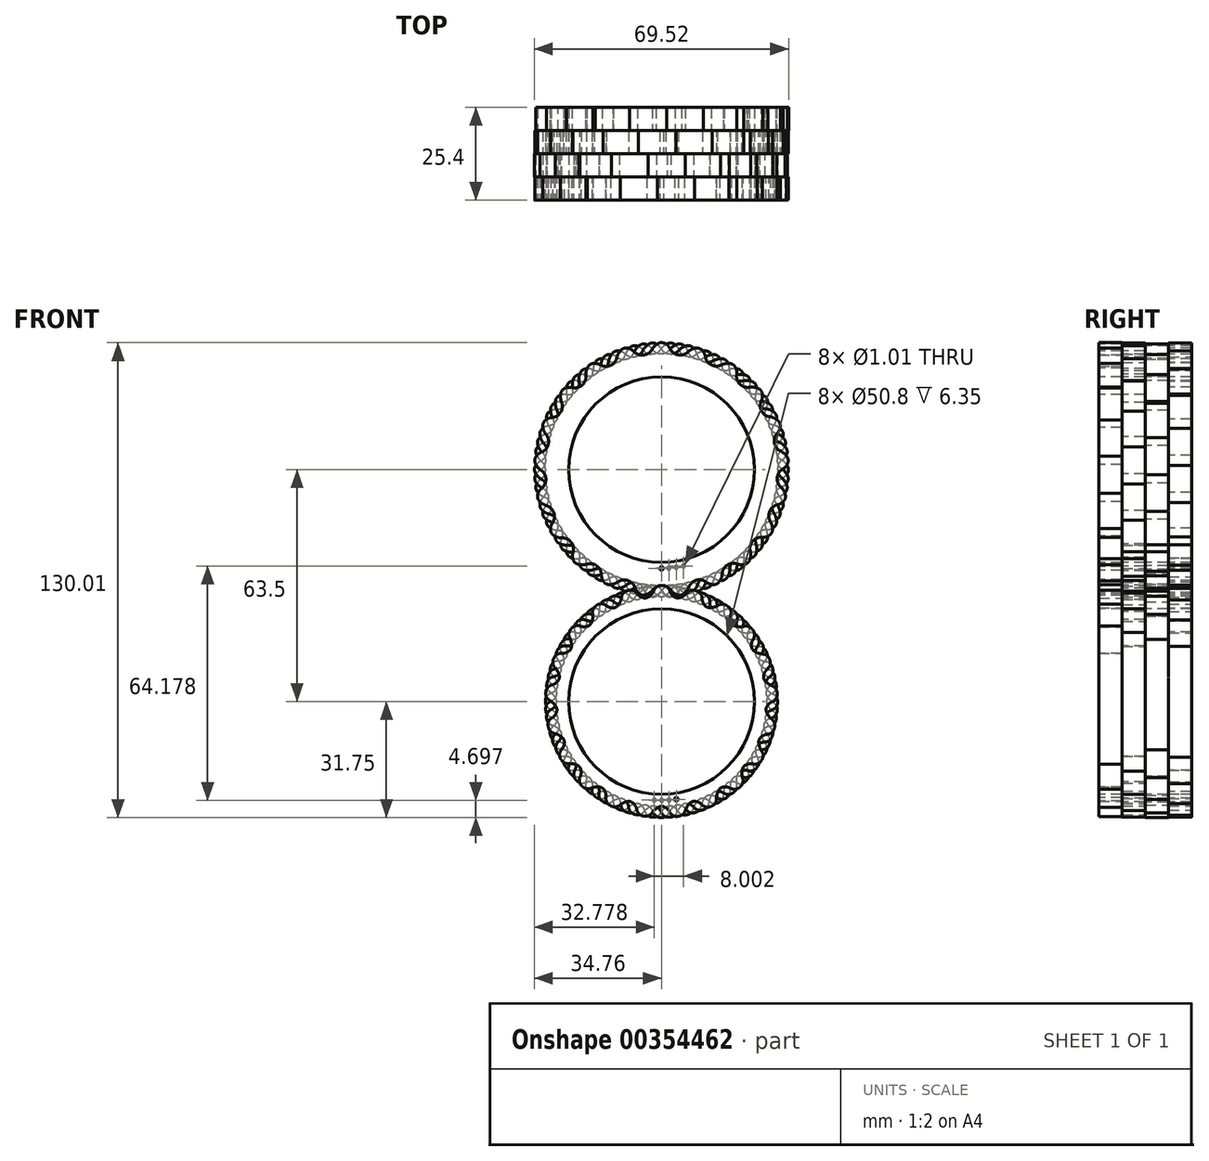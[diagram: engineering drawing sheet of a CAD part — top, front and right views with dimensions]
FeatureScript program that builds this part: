
annotation { "Feature Type Name" : "Feature", "Feature Type Description" : "" }
export const myFeature = defineFeature(function(context is Context, id is Id, definition is map)
    precondition{}
    {
        {
            var Q0;
            Q0=qCreatedBy(makeId("Front.planeOp"),FACE);
            var sketch = newSketch(context, id + "F0", { "sketchPlane" : qUnion([Q0])});
            skCircle(sketch, "E0", {"center": v(0, 0) * mm, "radius": 31.75 * mm});
            skCircle(sketch, "E1", {"center": v(0, 0) * mm, "radius": 25.4 * mm});
            skArc(sketch, "E2", {"start": v(0, 34.92) * mm, "mid": v(-2.02, 33.68) * mm, "end": v(-3.17, 31.6) * mm});
            skArc(sketch, "E3", {"start": v(0, 28.57) * mm, "mid": v(1.96, 29.69) * mm, "end": v(3.17, 31.6) * mm});
            skLineSegment(sketch, "E4", {"start": v(1.98, 33.73) * mm, "end": v(3.17, 31.6) * mm});
            skArc(sketch, "E5", {"start": v(-2.01, 29.74) * mm, "mid": v(-2.47, 30.74) * mm, "end": v(-3.17, 31.6) * mm});
            skArc(sketch, "E6", {"start": v(1.98, 33.73) * mm, "mid": v(1.06, 34.45) * mm, "end": v(0, 34.92) * mm});
            skArc(sketch, "E7", {"start": v(-2.01, 29.74) * mm, "mid": v(-1.08, 29.03) * mm, "end": v(0, 28.57) * mm});
            skArc(sketch, "E8.1.0", {"start": v(-10.3, 33.37) * mm, "mid": v(-11.86, 31.58) * mm, "end": v(-12.34, 29.25) * mm});
            skArc(sketch, "E8.1.1", {"start": v(-8.05, 32.8) * mm, "mid": v(-9.14, 33.23) * mm, "end": v(-10.3, 33.37) * mm});
            skLineSegment(sketch, "E8.1.2", {"start": v(-8.05, 32.8) * mm, "end": v(-6.28, 31.12) * mm});
            skArc(sketch, "E8.1.3", {"start": v(-8.42, 27.3) * mm, "mid": v(-6.88, 28.95) * mm, "end": v(-6.28, 31.12) * mm});
            skArc(sketch, "E8.1.4", {"start": v(-10.69, 27.82) * mm, "mid": v(-9.59, 27.42) * mm, "end": v(-8.42, 27.3) * mm});
            skArc(sketch, "E8.1.5", {"start": v(-10.69, 27.82) * mm, "mid": v(-11.42, 28.65) * mm, "end": v(-12.34, 29.25) * mm});
            skArc(sketch, "E8.2.0", {"start": v(-19.67, 28.86) * mm, "mid": v(-20.64, 26.68) * mm, "end": v(-20.42, 24.32) * mm});
            skArc(sketch, "E8.2.1", {"start": v(-17.37, 28.98) * mm, "mid": v(-18.53, 29.06) * mm, "end": v(-19.67, 28.86) * mm});
            skLineSegment(sketch, "E8.2.2", {"start": v(-17.37, 28.98) * mm, "end": v(-15.18, 27.89) * mm});
            skArc(sketch, "E8.2.3", {"start": v(-16.1, 23.6) * mm, "mid": v(-15.1, 25.63) * mm, "end": v(-15.18, 27.89) * mm});
            skArc(sketch, "E8.2.4", {"start": v(-18.41, 23.44) * mm, "mid": v(-17.24, 23.38) * mm, "end": v(-16.1, 23.6) * mm});
            skArc(sketch, "E8.2.5", {"start": v(-18.41, 23.44) * mm, "mid": v(-19.36, 24) * mm, "end": v(-20.42, 24.32) * mm});
            skArc(sketch, "E9.3.3.0", {"start": v(-27.3, 21.78) * mm, "mid": v(-27.6, 19.41) * mm, "end": v(-26.68, 17.22) * mm});
            skArc(sketch, "E9.4.3.0", {"start": v(-25.14, 22.57) * mm, "mid": v(-26.27, 22.31) * mm, "end": v(-27.3, 21.78) * mm});
            skLineSegment(sketch, "E9.8.3.0", {"start": v(-25.14, 22.57) * mm, "end": v(-22.72, 22.18) * mm});
            skArc(sketch, "E9.11.3.0", {"start": v(-22.34, 17.82) * mm, "mid": v(-21.99, 20.04) * mm, "end": v(-22.72, 22.18) * mm});
            skArc(sketch, "E9.15.3.0", {"start": v(-24.5, 16.97) * mm, "mid": v(-23.37, 17.26) * mm, "end": v(-22.34, 17.82) * mm});
            skArc(sketch, "E9.19.3.0", {"start": v(-24.5, 16.97) * mm, "mid": v(-25.57, 17.24) * mm, "end": v(-26.68, 17.22) * mm});
            skArc(sketch, "E9.3.4.0", {"start": v(-32.51, 12.76) * mm, "mid": v(-32.09, 10.42) * mm, "end": v(-30.57, 8.59) * mm});
            skArc(sketch, "E9.4.4.0", {"start": v(-30.67, 14.16) * mm, "mid": v(-31.68, 13.58) * mm, "end": v(-32.51, 12.76) * mm});
            skLineSegment(sketch, "E9.8.4.0", {"start": v(-30.67, 14.16) * mm, "end": v(-28.25, 14.5) * mm});
            skArc(sketch, "E9.11.4.0", {"start": v(-26.6, 10.44) * mm, "mid": v(-26.92, 12.67) * mm, "end": v(-28.25, 14.5) * mm});
            skArc(sketch, "E9.15.4.0", {"start": v(-28.42, 9) * mm, "mid": v(-27.42, 9.6) * mm, "end": v(-26.6, 10.44) * mm});
            skArc(sketch, "E9.19.4.0", {"start": v(-28.42, 9) * mm, "mid": v(-29.52, 8.93) * mm, "end": v(-30.57, 8.59) * mm});
            skArc(sketch, "E9.3.5.0", {"start": v(-34.83, 2.6) * mm, "mid": v(-33.73, 0.5) * mm, "end": v(-31.74, -0.8) * mm});
            skArc(sketch, "E9.4.5.0", {"start": v(-33.48, 4.5) * mm, "mid": v(-34.27, 3.63) * mm, "end": v(-34.83, 2.6) * mm});
            skLineSegment(sketch, "E9.8.5.0", {"start": v(-33.48, 4.5) * mm, "end": v(-31.27, 5.52) * mm});
            skArc(sketch, "E9.11.5.0", {"start": v(-28.5, 2.14) * mm, "mid": v(-29.46, 4.17) * mm, "end": v(-31.27, 5.52) * mm});
            skArc(sketch, "E9.15.5.0", {"start": v(-29.8, 0.22) * mm, "mid": v(-29.03, 1.1) * mm, "end": v(-28.5, 2.14) * mm});
            skArc(sketch, "E9.19.5.0", {"start": v(-29.8, 0.22) * mm, "mid": v(-30.84, -0.16) * mm, "end": v(-31.74, -0.8) * mm});
            skArc(sketch, "E9.3.6.0", {"start": v(-34.05, -7.77) * mm, "mid": v(-32.38, -9.47) * mm, "end": v(-30.1, -10.12) * mm});
            skArc(sketch, "E9.4.6.0", {"start": v(-33.32, -5.58) * mm, "mid": v(-33.82, -6.63) * mm, "end": v(-34.05, -7.77) * mm});
            skLineSegment(sketch, "E9.8.6.0", {"start": v(-33.32, -5.58) * mm, "end": v(-31.5, -3.94) * mm});
            skArc(sketch, "E9.11.6.0", {"start": v(-27.86, -6.36) * mm, "mid": v(-29.38, -4.7) * mm, "end": v(-31.5, -3.94) * mm});
            skArc(sketch, "E9.15.6.0", {"start": v(-28.55, -8.58) * mm, "mid": v(-28.06, -7.51) * mm, "end": v(-27.86, -6.36) * mm});
            skArc(sketch, "E9.19.6.0", {"start": v(-28.55, -8.58) * mm, "mid": v(-29.42, -9.25) * mm, "end": v(-30.1, -10.12) * mm});
            skArc(sketch, "E9.3.7.0", {"start": v(-30.25, -17.46) * mm, "mid": v(-28.15, -18.6) * mm, "end": v(-25.77, -18.54) * mm});
            skArc(sketch, "E9.4.7.0", {"start": v(-30.2, -15.15) * mm, "mid": v(-30.37, -16.3) * mm, "end": v(-30.25, -17.46) * mm});
            skLineSegment(sketch, "E9.8.7.0", {"start": v(-30.2, -15.15) * mm, "end": v(-28.94, -13.05) * mm});
            skArc(sketch, "E9.11.7.0", {"start": v(-24.75, -14.29) * mm, "mid": v(-26.7, -13.15) * mm, "end": v(-28.94, -13.05) * mm});
            skArc(sketch, "E9.15.7.0", {"start": v(-24.75, -16.61) * mm, "mid": v(-24.6, -15.45) * mm, "end": v(-24.75, -14.29) * mm});
            skArc(sketch, "E9.19.7.0", {"start": v(-24.75, -16.61) * mm, "mid": v(-25.39, -17.5) * mm, "end": v(-25.77, -18.54) * mm});
            skArc(sketch, "E9.3.8.0", {"start": v(-23.76, -25.6) * mm, "mid": v(-21.42, -26.06) * mm, "end": v(-19.16, -25.31) * mm});
            skArc(sketch, "E9.4.8.0", {"start": v(-24.39, -23.38) * mm, "mid": v(-24.21, -24.53) * mm, "end": v(-23.76, -25.6) * mm});
            skLineSegment(sketch, "E9.8.8.0", {"start": v(-24.39, -23.38) * mm, "end": v(-23.81, -21) * mm});
            skArc(sketch, "E9.11.8.0", {"start": v(-19.44, -20.95) * mm, "mid": v(-21.63, -20.43) * mm, "end": v(-23.81, -21) * mm});
            skArc(sketch, "E9.15.8.0", {"start": v(-18.75, -23.17) * mm, "mid": v(-18.95, -22.01) * mm, "end": v(-19.44, -20.95) * mm});
            skArc(sketch, "E9.19.8.0", {"start": v(-18.75, -23.17) * mm, "mid": v(-19.1, -24.21) * mm, "end": v(-19.16, -25.31) * mm});
            skArc(sketch, "E9.3.9.0", {"start": v(-15.15, -31.47) * mm, "mid": v(-12.79, -31.22) * mm, "end": v(-10.85, -29.84) * mm});
            skArc(sketch, "E9.4.9.0", {"start": v(-16.41, -29.53) * mm, "mid": v(-15.9, -30.58) * mm, "end": v(-15.15, -31.47) * mm});
            skLineSegment(sketch, "E9.8.9.0", {"start": v(-16.41, -29.53) * mm, "end": v(-16.56, -27.09) * mm});
            skArc(sketch, "E9.11.9.0", {"start": v(-12.4, -25.75) * mm, "mid": v(-14.65, -25.9) * mm, "end": v(-16.56, -27.09) * mm});
            skArc(sketch, "E9.15.9.0", {"start": v(-11.1, -27.67) * mm, "mid": v(-11.62, -26.62) * mm, "end": v(-12.4, -25.75) * mm});
            skArc(sketch, "E9.19.9.0", {"start": v(-11.1, -27.67) * mm, "mid": v(-11.11, -28.77) * mm, "end": v(-10.85, -29.84) * mm});
            skArc(sketch, "E9.3.10.0", {"start": v(-5.2, -34.53) * mm, "mid": v(-3.02, -33.6) * mm, "end": v(-1.57, -31.71) * mm});
            skArc(sketch, "E9.4.10.0", {"start": v(-6.98, -33.05) * mm, "mid": v(-6.19, -33.9) * mm, "end": v(-5.2, -34.53) * mm});
            skLineSegment(sketch, "E9.8.10.0", {"start": v(-6.98, -33.05) * mm, "end": v(-7.84, -30.77) * mm});
            skArc(sketch, "E9.11.10.0", {"start": v(-4.26, -28.26) * mm, "mid": v(-6.36, -29.07) * mm, "end": v(-7.84, -30.77) * mm});
            skArc(sketch, "E9.15.10.0", {"start": v(-2.44, -29.7) * mm, "mid": v(-3.26, -28.87) * mm, "end": v(-4.26, -28.26) * mm});
            skArc(sketch, "E9.19.10.0", {"start": v(-2.44, -29.7) * mm, "mid": v(-2.14, -30.77) * mm, "end": v(-1.57, -31.71) * mm});
            skArc(sketch, "E9.3.11.0", {"start": v(5.2, -34.53) * mm, "mid": v(7.02, -33) * mm, "end": v(7.84, -30.77) * mm});
            skArc(sketch, "E9.4.11.0", {"start": v(3.07, -33.64) * mm, "mid": v(4.08, -34.22) * mm, "end": v(5.2, -34.53) * mm});
            skLineSegment(sketch, "E9.8.11.0", {"start": v(3.07, -33.64) * mm, "end": v(1.57, -31.71) * mm});
            skArc(sketch, "E9.11.11.0", {"start": v(4.26, -28.26) * mm, "mid": v(2.49, -29.65) * mm, "end": v(1.57, -31.71) * mm});
            skArc(sketch, "E9.15.11.0", {"start": v(6.42, -29.1) * mm, "mid": v(5.4, -28.54) * mm, "end": v(4.26, -28.26) * mm});
            skArc(sketch, "E9.19.11.0", {"start": v(6.42, -29.1) * mm, "mid": v(7.02, -30.03) * mm, "end": v(7.84, -30.77) * mm});
            skArc(sketch, "E9.3.12.0", {"start": v(15.15, -31.47) * mm, "mid": v(16.43, -29.46) * mm, "end": v(16.56, -27.09) * mm});
            skArc(sketch, "E9.4.12.0", {"start": v(12.85, -31.24) * mm, "mid": v(13.99, -31.5) * mm, "end": v(15.15, -31.47) * mm});
            skLineSegment(sketch, "E9.8.12.0", {"start": v(12.85, -31.24) * mm, "end": v(10.85, -29.84) * mm});
            skArc(sketch, "E9.11.12.0", {"start": v(12.4, -25.75) * mm, "mid": v(11.12, -27.6) * mm, "end": v(10.85, -29.84) * mm});
            skArc(sketch, "E9.15.12.0", {"start": v(14.72, -25.92) * mm, "mid": v(13.57, -25.69) * mm, "end": v(12.4, -25.75) * mm});
            skArc(sketch, "E9.19.12.0", {"start": v(14.72, -25.92) * mm, "mid": v(15.56, -26.63) * mm, "end": v(16.56, -27.09) * mm});
            skArc(sketch, "E9.3.13.0", {"start": v(23.76, -25.6) * mm, "mid": v(24.39, -23.3) * mm, "end": v(23.81, -21) * mm});
            skArc(sketch, "E9.4.13.0", {"start": v(21.5, -26.07) * mm, "mid": v(22.65, -25.98) * mm, "end": v(23.76, -25.6) * mm});
            skLineSegment(sketch, "E9.8.13.0", {"start": v(21.5, -26.07) * mm, "end": v(19.16, -25.31) * mm});
            skArc(sketch, "E9.11.13.0", {"start": v(19.44, -20.95) * mm, "mid": v(18.76, -23.1) * mm, "end": v(19.16, -25.31) * mm});
            skArc(sketch, "E9.15.13.0", {"start": v(21.7, -20.43) * mm, "mid": v(20.54, -20.55) * mm, "end": v(19.44, -20.95) * mm});
            skArc(sketch, "E9.19.13.0", {"start": v(21.7, -20.43) * mm, "mid": v(22.72, -20.86) * mm, "end": v(23.81, -21) * mm});
            skArc(sketch, "E9.3.14.0", {"start": v(30.25, -17.46) * mm, "mid": v(30.18, -15.08) * mm, "end": v(28.94, -13.05) * mm});
            skArc(sketch, "E9.4.14.0", {"start": v(28.22, -18.57) * mm, "mid": v(29.3, -18.15) * mm, "end": v(30.25, -17.46) * mm});
            skLineSegment(sketch, "E9.8.14.0", {"start": v(28.22, -18.57) * mm, "end": v(25.77, -18.54) * mm});
            skArc(sketch, "E9.11.14.0", {"start": v(24.75, -14.29) * mm, "mid": v(24.73, -16.54) * mm, "end": v(25.77, -18.54) * mm});
            skArc(sketch, "E9.15.14.0", {"start": v(26.76, -13.13) * mm, "mid": v(25.68, -13.58) * mm, "end": v(24.75, -14.29) * mm});
            skArc(sketch, "E9.19.14.0", {"start": v(26.76, -13.13) * mm, "mid": v(27.86, -13.23) * mm, "end": v(28.94, -13.05) * mm});
            skArc(sketch, "E9.3.15.0", {"start": v(34.05, -7.77) * mm, "mid": v(33.28, -5.52) * mm, "end": v(31.5, -3.94) * mm});
            skArc(sketch, "E9.4.15.0", {"start": v(32.44, -9.43) * mm, "mid": v(33.35, -8.7) * mm, "end": v(34.05, -7.77) * mm});
            skLineSegment(sketch, "E9.8.15.0", {"start": v(32.44, -9.43) * mm, "end": v(30.1, -10.12) * mm});
            skArc(sketch, "E9.11.15.0", {"start": v(27.86, -6.36) * mm, "mid": v(28.5, -8.52) * mm, "end": v(30.1, -10.12) * mm});
            skArc(sketch, "E9.15.15.0", {"start": v(29.44, -4.66) * mm, "mid": v(28.54, -5.4) * mm, "end": v(27.86, -6.36) * mm});
            skArc(sketch, "E9.19.15.0", {"start": v(29.44, -4.66) * mm, "mid": v(30.52, -4.43) * mm, "end": v(31.5, -3.94) * mm});
            skArc(sketch, "E9.3.16.0", {"start": v(34.83, 2.6) * mm, "mid": v(33.43, 4.54) * mm, "end": v(31.27, 5.52) * mm});
            skArc(sketch, "E9.4.16.0", {"start": v(33.78, 0.55) * mm, "mid": v(34.43, 1.51) * mm, "end": v(34.83, 2.6) * mm});
            skLineSegment(sketch, "E9.8.16.0", {"start": v(33.78, 0.55) * mm, "end": v(31.74, -0.8) * mm});
            skArc(sketch, "E9.11.16.0", {"start": v(28.5, 2.14) * mm, "mid": v(29.75, 0.26) * mm, "end": v(31.74, -0.8) * mm});
            skArc(sketch, "E9.15.16.0", {"start": v(29.5, 4.23) * mm, "mid": v(28.87, 3.25) * mm, "end": v(28.5, 2.14) * mm});
            skArc(sketch, "E9.19.16.0", {"start": v(29.5, 4.23) * mm, "mid": v(30.47, 4.76) * mm, "end": v(31.27, 5.52) * mm});
            skArc(sketch, "E9.3.17.0", {"start": v(32.51, 12.76) * mm, "mid": v(30.6, 14.19) * mm, "end": v(28.25, 14.5) * mm});
            skArc(sketch, "E9.4.17.0", {"start": v(32.12, 10.48) * mm, "mid": v(32.46, 11.6) * mm, "end": v(32.51, 12.76) * mm});
            skLineSegment(sketch, "E9.8.17.0", {"start": v(32.12, 10.48) * mm, "end": v(30.57, 8.59) * mm});
            skArc(sketch, "E9.11.17.0", {"start": v(26.6, 10.44) * mm, "mid": v(28.35, 9.02) * mm, "end": v(30.57, 8.59) * mm});
            skArc(sketch, "E9.15.17.0", {"start": v(26.95, 12.74) * mm, "mid": v(26.63, 11.61) * mm, "end": v(26.6, 10.44) * mm});
            skArc(sketch, "E9.19.17.0", {"start": v(26.95, 12.74) * mm, "mid": v(27.72, 13.53) * mm, "end": v(28.25, 14.5) * mm});
            skArc(sketch, "E9.3.18.0", {"start": v(27.3, 21.78) * mm, "mid": v(25.07, 22.58) * mm, "end": v(22.72, 22.18) * mm});
            skArc(sketch, "E9.4.18.0", {"start": v(27.6, 19.48) * mm, "mid": v(27.6, 20.65) * mm, "end": v(27.3, 21.78) * mm});
            skLineSegment(sketch, "E9.8.18.0", {"start": v(27.6, 19.48) * mm, "end": v(26.68, 17.22) * mm});
            skArc(sketch, "E9.11.18.0", {"start": v(22.34, 17.82) * mm, "mid": v(24.43, 16.98) * mm, "end": v(26.68, 17.22) * mm});
            skArc(sketch, "E9.15.18.0", {"start": v(22, 20.11) * mm, "mid": v(22.02, 18.94) * mm, "end": v(22.34, 17.82) * mm});
            skArc(sketch, "E9.19.18.0", {"start": v(22, 20.11) * mm, "mid": v(22.5, 21.1) * mm, "end": v(22.72, 22.18) * mm});
            skArc(sketch, "E9.3.19.0", {"start": v(19.67, 28.86) * mm, "mid": v(17.3, 28.96) * mm, "end": v(15.18, 27.89) * mm});
            skArc(sketch, "E9.4.19.0", {"start": v(20.63, 26.75) * mm, "mid": v(20.28, 27.86) * mm, "end": v(19.67, 28.86) * mm});
            skLineSegment(sketch, "E9.8.19.0", {"start": v(20.63, 26.75) * mm, "end": v(20.42, 24.32) * mm});
            skArc(sketch, "E9.11.19.0", {"start": v(16.1, 23.6) * mm, "mid": v(18.34, 23.43) * mm, "end": v(20.42, 24.32) * mm});
            skArc(sketch, "E9.15.19.0", {"start": v(15.1, 25.7) * mm, "mid": v(15.46, 24.6) * mm, "end": v(16.1, 23.6) * mm});
            skArc(sketch, "E9.19.19.0", {"start": v(15.1, 25.7) * mm, "mid": v(15.28, 26.8) * mm, "end": v(15.18, 27.89) * mm});
            skArc(sketch, "E9.3.20.0", {"start": v(10.3, 33.37) * mm, "mid": v(8, 32.78) * mm, "end": v(6.28, 31.12) * mm});
            skArc(sketch, "E9.4.20.0", {"start": v(11.83, 31.64) * mm, "mid": v(11.17, 32.6) * mm, "end": v(10.3, 33.37) * mm});
            skLineSegment(sketch, "E9.8.20.0", {"start": v(11.83, 31.64) * mm, "end": v(12.34, 29.25) * mm});
            skArc(sketch, "E9.11.20.0", {"start": v(8.42, 27.3) * mm, "mid": v(10.62, 27.8) * mm, "end": v(12.34, 29.25) * mm});
            skArc(sketch, "E9.15.20.0", {"start": v(6.84, 29.01) * mm, "mid": v(7.53, 28.06) * mm, "end": v(8.42, 27.3) * mm});
            skArc(sketch, "E9.19.20.0", {"start": v(6.84, 29.01) * mm, "mid": v(6.7, 30.1) * mm, "end": v(6.28, 31.12) * mm});
            skArc(sketch, "E10", {"start": v(0.11, 34.89) * mm, "mid": v(-0.54, 34.69) * mm, "end": v(-1.15, 34.4) * mm});
            skArc(sketch, "E11.1.0", {"start": v(-10.18, 33.37) * mm, "mid": v(-10.74, 32.99) * mm, "end": v(-11.24, 32.53) * mm});
            skArc(sketch, "E11.2.0", {"start": v(-19.56, 28.89) * mm, "mid": v(-19.99, 28.36) * mm, "end": v(-20.33, 27.77) * mm});
            skArc(sketch, "E11.3.0", {"start": v(-27.2, 21.84) * mm, "mid": v(-27.46, 21.2) * mm, "end": v(-27.6, 20.54) * mm});
            skArc(sketch, "E11.4.0", {"start": v(-32.44, 12.85) * mm, "mid": v(-32.49, 12.17) * mm, "end": v(-32.44, 11.5) * mm});
            skArc(sketch, "E11.5.0", {"start": v(-34.78, 2.72) * mm, "mid": v(-34.63, 2.05) * mm, "end": v(-34.38, 1.42) * mm});
            skArc(sketch, "E11.6.0", {"start": v(-34.04, -7.66) * mm, "mid": v(-33.7, -8.24) * mm, "end": v(-33.28, -8.78) * mm});
            skArc(sketch, "E11.7.0", {"start": v(-30.27, -17.35) * mm, "mid": v(-29.77, -17.81) * mm, "end": v(-29.21, -18.2) * mm});
            skArc(sketch, "E11.8.0", {"start": v(-23.81, -25.5) * mm, "mid": v(-23.2, -25.8) * mm, "end": v(-22.55, -26) * mm});
            skArc(sketch, "E11.9.0", {"start": v(-15.24, -31.39) * mm, "mid": v(-14.56, -31.49) * mm, "end": v(-13.89, -31.49) * mm});
            skArc(sketch, "E11.10.0", {"start": v(-5.3, -34.48) * mm, "mid": v(-4.64, -34.38) * mm, "end": v(-3.99, -34.18) * mm});
            skArc(sketch, "E11.11.0", {"start": v(5.1, -34.52) * mm, "mid": v(5.7, -34.22) * mm, "end": v(6.27, -33.84) * mm});
            skArc(sketch, "E11.12.0", {"start": v(15.04, -31.48) * mm, "mid": v(15.54, -31.02) * mm, "end": v(15.96, -30.49) * mm});
            skArc(sketch, "E11.13.0", {"start": v(23.65, -25.65) * mm, "mid": v(23.99, -25.06) * mm, "end": v(24.24, -24.43) * mm});
            skArc(sketch, "E11.14.0", {"start": v(30.16, -17.54) * mm, "mid": v(30.31, -16.88) * mm, "end": v(30.36, -16.2) * mm});
            skArc(sketch, "E11.15.0", {"start": v(34, -7.87) * mm, "mid": v(33.94, -7.2) * mm, "end": v(33.79, -6.53) * mm});
            skArc(sketch, "E11.16.0", {"start": v(34.8, 2.5) * mm, "mid": v(34.55, 3.13) * mm, "end": v(34.21, 3.72) * mm});
            skArc(sketch, "E11.17.0", {"start": v(32.52, 12.64) * mm, "mid": v(32.1, 13.17) * mm, "end": v(31.6, 13.64) * mm});
            skArc(sketch, "E11.18.0", {"start": v(27.35, 21.67) * mm, "mid": v(26.78, 22.05) * mm, "end": v(26.17, 22.34) * mm});
            skArc(sketch, "E11.19.0", {"start": v(19.75, 28.77) * mm, "mid": v(19.1, 28.96) * mm, "end": v(18.42, 29.07) * mm});
            skArc(sketch, "E11.20.0", {"start": v(10.39, 33.3) * mm, "mid": v(9.7, 33.3) * mm, "end": v(9.04, 33.2) * mm});
            skCircle(sketch, "E12", {"center": v(0, -27.05) * mm, "radius": 0.5 * mm});
            skSolve(sketch);
        }
        {
            var Q0;
            Q0=makeQuery(id+"F0.imprint","IMPRINT",FACE,{"disambiguationData":[TD([[makeQuery(id+"F0.imprint","IMPRINT",EDGE,{"derivedFrom":sQuery(id+"F0.wireOp",EDGE,"E1")}),-1.0]])]});
            var Q1;
            Q1=makeQuery(id+"F0.imprint","IMPRINT",FACE,{"disambiguationData":[TD([[makeQuery(id+"F0.imprint","IMPRINT",EDGE,{"derivedFrom":sQuery(id+"F0.wireOp",EDGE,"Dn7gvafj-PEvj-KMcr-wK7N-n03crIEQc72X")}),1.0]])]});
            extrude(context, id + "F1", {"entities" : qUnion([Q0, Q1]), "oppositeDirection" : true, "depth" : 6.35 * mm});
        }
        {
            var Q0;
            {var subQ2=sQuery(id+"F0.wireOp",EDGE,"E3");Q0=makeQuery(id+"F0.imprint","IMPRINT",FACE,{"disambiguationData":[TD([[makeQuery(id+"F0.imprint","IMPRINT",EDGE,{"derivedFrom":subQ2}),1.0]])]});}
            var Q1;
            {var subQ2=sQuery(id+"F0.wireOp",EDGE,"E9.11.20.0");Q1=makeQuery(id+"F0.imprint","IMPRINT",FACE,{"disambiguationData":[TD([[makeQuery(id+"F0.imprint","IMPRINT",EDGE,{"derivedFrom":subQ2}),1.0]])]});}
            var Q2;
            {var subQ2=sQuery(id+"F0.wireOp",EDGE,"E9.11.19.0");Q2=makeQuery(id+"F0.imprint","IMPRINT",FACE,{"disambiguationData":[TD([[makeQuery(id+"F0.imprint","IMPRINT",EDGE,{"derivedFrom":subQ2}),1.0]])]});}
            var Q3;
            {var subQ2=sQuery(id+"F0.wireOp",EDGE,"E9.11.18.0");Q3=makeQuery(id+"F0.imprint","IMPRINT",FACE,{"disambiguationData":[TD([[makeQuery(id+"F0.imprint","IMPRINT",EDGE,{"derivedFrom":subQ2}),1.0]])]});}
            var Q4;
            {var subQ2=sQuery(id+"F0.wireOp",EDGE,"E8.1.3");Q4=makeQuery(id+"F0.imprint","IMPRINT",FACE,{"disambiguationData":[TD([[makeQuery(id+"F0.imprint","IMPRINT",EDGE,{"derivedFrom":subQ2}),1.0]])]});}
            var Q5;
            {var subQ2=sQuery(id+"F0.wireOp",EDGE,"E8.2.3");Q5=makeQuery(id+"F0.imprint","IMPRINT",FACE,{"disambiguationData":[TD([[makeQuery(id+"F0.imprint","IMPRINT",EDGE,{"derivedFrom":subQ2}),1.0]])]});}
            var Q6;
            {var subQ2=sQuery(id+"F0.wireOp",EDGE,"E9.11.3.0");Q6=makeQuery(id+"F0.imprint","IMPRINT",FACE,{"disambiguationData":[TD([[makeQuery(id+"F0.imprint","IMPRINT",EDGE,{"derivedFrom":subQ2}),1.0]])]});}
            var Q7;
            {var subQ2=sQuery(id+"F0.wireOp",EDGE,"E9.11.4.0");Q7=makeQuery(id+"F0.imprint","IMPRINT",FACE,{"disambiguationData":[TD([[makeQuery(id+"F0.imprint","IMPRINT",EDGE,{"derivedFrom":subQ2}),1.0]])]});}
            var Q8;
            {var subQ2=sQuery(id+"F0.wireOp",EDGE,"E9.11.5.0");Q8=makeQuery(id+"F0.imprint","IMPRINT",FACE,{"disambiguationData":[TD([[makeQuery(id+"F0.imprint","IMPRINT",EDGE,{"derivedFrom":subQ2}),1.0]])]});}
            var Q9;
            {var subQ2=sQuery(id+"F0.wireOp",EDGE,"E9.11.6.0");Q9=makeQuery(id+"F0.imprint","IMPRINT",FACE,{"disambiguationData":[TD([[makeQuery(id+"F0.imprint","IMPRINT",EDGE,{"derivedFrom":subQ2}),1.0]])]});}
            var Q10;
            {var subQ2=sQuery(id+"F0.wireOp",EDGE,"E9.11.17.0");Q10=makeQuery(id+"F0.imprint","IMPRINT",FACE,{"disambiguationData":[TD([[makeQuery(id+"F0.imprint","IMPRINT",EDGE,{"derivedFrom":subQ2}),1.0]])]});}
            var Q11;
            {var subQ2=sQuery(id+"F0.wireOp",EDGE,"E9.11.16.0");Q11=makeQuery(id+"F0.imprint","IMPRINT",FACE,{"disambiguationData":[TD([[makeQuery(id+"F0.imprint","IMPRINT",EDGE,{"derivedFrom":subQ2}),1.0]])]});}
            var Q12;
            {var subQ2=sQuery(id+"F0.wireOp",EDGE,"E9.11.15.0");Q12=makeQuery(id+"F0.imprint","IMPRINT",FACE,{"disambiguationData":[TD([[makeQuery(id+"F0.imprint","IMPRINT",EDGE,{"derivedFrom":subQ2}),1.0]])]});}
            var Q13;
            {var subQ2=sQuery(id+"F0.wireOp",EDGE,"E9.11.7.0");Q13=makeQuery(id+"F0.imprint","IMPRINT",FACE,{"disambiguationData":[TD([[makeQuery(id+"F0.imprint","IMPRINT",EDGE,{"derivedFrom":subQ2}),1.0]])]});}
            var Q14;
            {var subQ2=sQuery(id+"F0.wireOp",EDGE,"E9.11.8.0");Q14=makeQuery(id+"F0.imprint","IMPRINT",FACE,{"disambiguationData":[TD([[makeQuery(id+"F0.imprint","IMPRINT",EDGE,{"derivedFrom":subQ2}),1.0]])]});}
            var Q15;
            {var subQ2=sQuery(id+"F0.wireOp",EDGE,"E9.11.9.0");Q15=makeQuery(id+"F0.imprint","IMPRINT",FACE,{"disambiguationData":[TD([[makeQuery(id+"F0.imprint","IMPRINT",EDGE,{"derivedFrom":subQ2}),1.0]])]});}
            var Q16;
            {var subQ2=sQuery(id+"F0.wireOp",EDGE,"E9.11.10.0");Q16=makeQuery(id+"F0.imprint","IMPRINT",FACE,{"disambiguationData":[TD([[makeQuery(id+"F0.imprint","IMPRINT",EDGE,{"derivedFrom":subQ2}),1.0]])]});}
            var Q17;
            {var subQ2=sQuery(id+"F0.wireOp",EDGE,"E9.11.11.0");Q17=makeQuery(id+"F0.imprint","IMPRINT",FACE,{"disambiguationData":[TD([[makeQuery(id+"F0.imprint","IMPRINT",EDGE,{"derivedFrom":subQ2}),1.0]])]});}
            var Q18;
            {var subQ2=sQuery(id+"F0.wireOp",EDGE,"E9.11.12.0");Q18=makeQuery(id+"F0.imprint","IMPRINT",FACE,{"disambiguationData":[TD([[makeQuery(id+"F0.imprint","IMPRINT",EDGE,{"derivedFrom":subQ2}),1.0]])]});}
            var Q19;
            {var subQ2=sQuery(id+"F0.wireOp",EDGE,"E9.11.13.0");Q19=makeQuery(id+"F0.imprint","IMPRINT",FACE,{"disambiguationData":[TD([[makeQuery(id+"F0.imprint","IMPRINT",EDGE,{"derivedFrom":subQ2}),1.0]])]});}
            var Q20;
            {var subQ2=sQuery(id+"F0.wireOp",EDGE,"E9.11.14.0");Q20=makeQuery(id+"F0.imprint","IMPRINT",FACE,{"disambiguationData":[TD([[makeQuery(id+"F0.imprint","IMPRINT",EDGE,{"derivedFrom":subQ2}),1.0]])]});}
            var Q21;
            Q21=makeQuery(id+"F0.imprint","IMPRINT",FACE,{"disambiguationData":[TD([[makeQuery(id+"F0.imprint","IMPRINT",EDGE,{"derivedFrom":sQuery(id+"F0.wireOp",EDGE,"E1")}),-1.0]])]});
            var Q22;
            {var subQ1=sQuery(id+"F0.wireOp",EDGE,"E4");Q22=makeQuery(id+"F0.imprint","IMPRINT",FACE,{"disambiguationData":[TD([[makeQuery(id+"F0.imprint","IMPRINT",EDGE,{"derivedFrom":subQ1}),-1.0]])]});}
            var Q23;
            {var subQ0=sQuery(id+"F0.wireOp",EDGE,"E9.8.20.0");Q23=makeQuery(id+"F0.imprint","IMPRINT",FACE,{"disambiguationData":[TD([[makeQuery(id+"F0.imprint","IMPRINT",EDGE,{"derivedFrom":subQ0}),-1.0]])]});}
            var Q24;
            {var subQ0=sQuery(id+"F0.wireOp",EDGE,"E9.8.19.0");Q24=makeQuery(id+"F0.imprint","IMPRINT",FACE,{"disambiguationData":[TD([[makeQuery(id+"F0.imprint","IMPRINT",EDGE,{"derivedFrom":subQ0}),-1.0]])]});}
            var Q25;
            {var subQ0=sQuery(id+"F0.wireOp",EDGE,"E9.8.18.0");Q25=makeQuery(id+"F0.imprint","IMPRINT",FACE,{"disambiguationData":[TD([[makeQuery(id+"F0.imprint","IMPRINT",EDGE,{"derivedFrom":subQ0}),-1.0]])]});}
            var Q26;
            {var subQ0=sQuery(id+"F0.wireOp",EDGE,"E9.8.17.0");Q26=makeQuery(id+"F0.imprint","IMPRINT",FACE,{"disambiguationData":[TD([[makeQuery(id+"F0.imprint","IMPRINT",EDGE,{"derivedFrom":subQ0}),-1.0]])]});}
            var Q27;
            {var subQ0=sQuery(id+"F0.wireOp",EDGE,"E9.8.16.0");Q27=makeQuery(id+"F0.imprint","IMPRINT",FACE,{"disambiguationData":[TD([[makeQuery(id+"F0.imprint","IMPRINT",EDGE,{"derivedFrom":subQ0}),-1.0]])]});}
            var Q28;
            {var subQ0=sQuery(id+"F0.wireOp",EDGE,"E9.8.15.0");Q28=makeQuery(id+"F0.imprint","IMPRINT",FACE,{"disambiguationData":[TD([[makeQuery(id+"F0.imprint","IMPRINT",EDGE,{"derivedFrom":subQ0}),-1.0]])]});}
            var Q29;
            {var subQ0=sQuery(id+"F0.wireOp",EDGE,"E9.8.14.0");Q29=makeQuery(id+"F0.imprint","IMPRINT",FACE,{"disambiguationData":[TD([[makeQuery(id+"F0.imprint","IMPRINT",EDGE,{"derivedFrom":subQ0}),-1.0]])]});}
            var Q30;
            {var subQ0=sQuery(id+"F0.wireOp",EDGE,"E9.8.13.0");Q30=makeQuery(id+"F0.imprint","IMPRINT",FACE,{"disambiguationData":[TD([[makeQuery(id+"F0.imprint","IMPRINT",EDGE,{"derivedFrom":subQ0}),-1.0]])]});}
            var Q31;
            {var subQ0=sQuery(id+"F0.wireOp",EDGE,"E9.8.12.0");Q31=makeQuery(id+"F0.imprint","IMPRINT",FACE,{"disambiguationData":[TD([[makeQuery(id+"F0.imprint","IMPRINT",EDGE,{"derivedFrom":subQ0}),-1.0]])]});}
            var Q32;
            {var subQ0=sQuery(id+"F0.wireOp",EDGE,"E9.8.11.0");Q32=makeQuery(id+"F0.imprint","IMPRINT",FACE,{"disambiguationData":[TD([[makeQuery(id+"F0.imprint","IMPRINT",EDGE,{"derivedFrom":subQ0}),-1.0]])]});}
            var Q33;
            {var subQ0=sQuery(id+"F0.wireOp",EDGE,"E9.8.10.0");Q33=makeQuery(id+"F0.imprint","IMPRINT",FACE,{"disambiguationData":[TD([[makeQuery(id+"F0.imprint","IMPRINT",EDGE,{"derivedFrom":subQ0}),-1.0]])]});}
            var Q34;
            {var subQ0=sQuery(id+"F0.wireOp",EDGE,"E9.8.9.0");Q34=makeQuery(id+"F0.imprint","IMPRINT",FACE,{"disambiguationData":[TD([[makeQuery(id+"F0.imprint","IMPRINT",EDGE,{"derivedFrom":subQ0}),-1.0]])]});}
            var Q35;
            {var subQ0=sQuery(id+"F0.wireOp",EDGE,"E9.8.8.0");Q35=makeQuery(id+"F0.imprint","IMPRINT",FACE,{"disambiguationData":[TD([[makeQuery(id+"F0.imprint","IMPRINT",EDGE,{"derivedFrom":subQ0}),-1.0]])]});}
            var Q36;
            {var subQ0=sQuery(id+"F0.wireOp",EDGE,"E9.8.7.0");Q36=makeQuery(id+"F0.imprint","IMPRINT",FACE,{"disambiguationData":[TD([[makeQuery(id+"F0.imprint","IMPRINT",EDGE,{"derivedFrom":subQ0}),-1.0]])]});}
            var Q37;
            {var subQ0=sQuery(id+"F0.wireOp",EDGE,"E9.8.6.0");Q37=makeQuery(id+"F0.imprint","IMPRINT",FACE,{"disambiguationData":[TD([[makeQuery(id+"F0.imprint","IMPRINT",EDGE,{"derivedFrom":subQ0}),-1.0]])]});}
            var Q38;
            {var subQ0=sQuery(id+"F0.wireOp",EDGE,"E9.8.5.0");Q38=makeQuery(id+"F0.imprint","IMPRINT",FACE,{"disambiguationData":[TD([[makeQuery(id+"F0.imprint","IMPRINT",EDGE,{"derivedFrom":subQ0}),-1.0]])]});}
            var Q39;
            {var subQ0=sQuery(id+"F0.wireOp",EDGE,"E9.8.4.0");Q39=makeQuery(id+"F0.imprint","IMPRINT",FACE,{"disambiguationData":[TD([[makeQuery(id+"F0.imprint","IMPRINT",EDGE,{"derivedFrom":subQ0}),-1.0]])]});}
            var Q40;
            {var subQ0=sQuery(id+"F0.wireOp",EDGE,"E9.8.3.0");Q40=makeQuery(id+"F0.imprint","IMPRINT",FACE,{"disambiguationData":[TD([[makeQuery(id+"F0.imprint","IMPRINT",EDGE,{"derivedFrom":subQ0}),-1.0]])]});}
            var Q41;
            {var subQ0=sQuery(id+"F0.wireOp",EDGE,"E8.2.2");Q41=makeQuery(id+"F0.imprint","IMPRINT",FACE,{"disambiguationData":[TD([[makeQuery(id+"F0.imprint","IMPRINT",EDGE,{"derivedFrom":subQ0}),-1.0]])]});}
            var Q42;
            {var subQ0=sQuery(id+"F0.wireOp",EDGE,"E8.1.2");Q42=makeQuery(id+"F0.imprint","IMPRINT",FACE,{"disambiguationData":[TD([[makeQuery(id+"F0.imprint","IMPRINT",EDGE,{"derivedFrom":subQ0}),-1.0]])]});}
            extrude(context, id + "F2", {"entities" : qUnion([Q0, Q1, Q2, Q3, Q4, Q5, Q6, Q7, Q8, Q9, Q10, Q11, Q12, Q13, Q14, Q15, Q16, Q17, Q18, Q19, Q20, Q21, Q22, Q23, Q24, Q25, Q26, Q27, Q28, Q29, Q30, Q31, Q32, Q33, Q34, Q35, Q36, Q37, Q38, Q39, Q40, Q41, Q42]), "oppositeDirection" : true, "depth" : 6.35 * mm});
        }
        {
            var Q0;
            Q0=makeQuery(id+"F2.opExtrude","SWEPT_EDGE",EDGE,{"disambiguationData":[OSD([sQuery(id+"F0.wireOp",EDGE,"E6"),sQuery(id+"F0.wireOp",EDGE,"E10")])]});
            var Q1;
            Q1=makeQuery(id+"F2.opExtrude","SWEPT_EDGE",EDGE,{"disambiguationData":[OSD([sQuery(id+"F0.wireOp",EDGE,"E8.1.1"),sQuery(id+"F0.wireOp",EDGE,"E11.1.0")])]});
            var Q2;
            Q2=makeQuery(id+"F2.opExtrude","SWEPT_EDGE",EDGE,{"disambiguationData":[OSD([sQuery(id+"F0.wireOp",EDGE,"E8.2.1"),sQuery(id+"F0.wireOp",EDGE,"E11.2.0")])]});
            var Q3;
            Q3=makeQuery(id+"F2.opExtrude","SWEPT_EDGE",EDGE,{"disambiguationData":[OSD([sQuery(id+"F0.wireOp",EDGE,"E9.4.3.0"),sQuery(id+"F0.wireOp",EDGE,"E11.3.0")])]});
            var Q4;
            Q4=makeQuery(id+"F2.opExtrude","SWEPT_EDGE",EDGE,{"disambiguationData":[OSD([sQuery(id+"F0.wireOp",EDGE,"E9.4.20.0"),sQuery(id+"F0.wireOp",EDGE,"E11.20.0")])]});
            var Q5;
            Q5=makeQuery(id+"F2.opExtrude","SWEPT_EDGE",EDGE,{"disambiguationData":[OSD([sQuery(id+"F0.wireOp",EDGE,"E9.4.19.0"),sQuery(id+"F0.wireOp",EDGE,"E11.19.0")])]});
            var Q6;
            Q6=makeQuery(id+"F2.opExtrude","SWEPT_EDGE",EDGE,{"disambiguationData":[OSD([sQuery(id+"F0.wireOp",EDGE,"E9.4.18.0"),sQuery(id+"F0.wireOp",EDGE,"E11.18.0")])]});
            var Q7;
            Q7=makeQuery(id+"F2.opExtrude","SWEPT_EDGE",EDGE,{"disambiguationData":[OSD([sQuery(id+"F0.wireOp",EDGE,"E9.4.17.0"),sQuery(id+"F0.wireOp",EDGE,"E11.17.0")])]});
            var Q8;
            Q8=makeQuery(id+"F2.opExtrude","SWEPT_EDGE",EDGE,{"disambiguationData":[OSD([sQuery(id+"F0.wireOp",EDGE,"E9.4.16.0"),sQuery(id+"F0.wireOp",EDGE,"E11.16.0")])]});
            var Q9;
            Q9=makeQuery(id+"F2.opExtrude","SWEPT_EDGE",EDGE,{"disambiguationData":[OSD([sQuery(id+"F0.wireOp",EDGE,"E9.4.15.0"),sQuery(id+"F0.wireOp",EDGE,"E11.15.0")])]});
            var Q10;
            Q10=makeQuery(id+"F2.opExtrude","SWEPT_EDGE",EDGE,{"disambiguationData":[OSD([sQuery(id+"F0.wireOp",EDGE,"E9.4.4.0"),sQuery(id+"F0.wireOp",EDGE,"E11.4.0")])]});
            var Q11;
            Q11=makeQuery(id+"F2.opExtrude","SWEPT_EDGE",EDGE,{"disambiguationData":[OSD([sQuery(id+"F0.wireOp",EDGE,"E9.4.5.0"),sQuery(id+"F0.wireOp",EDGE,"E11.5.0")])]});
            var Q12;
            Q12=makeQuery(id+"F2.opExtrude","SWEPT_EDGE",EDGE,{"disambiguationData":[OSD([sQuery(id+"F0.wireOp",EDGE,"E9.4.6.0"),sQuery(id+"F0.wireOp",EDGE,"E11.6.0")])]});
            var Q13;
            Q13=makeQuery(id+"F2.opExtrude","SWEPT_EDGE",EDGE,{"disambiguationData":[OSD([sQuery(id+"F0.wireOp",EDGE,"E9.4.7.0"),sQuery(id+"F0.wireOp",EDGE,"E11.7.0")])]});
            var Q14;
            Q14=makeQuery(id+"F2.opExtrude","SWEPT_EDGE",EDGE,{"disambiguationData":[OSD([sQuery(id+"F0.wireOp",EDGE,"E9.4.14.0"),sQuery(id+"F0.wireOp",EDGE,"E11.14.0")])]});
            var Q15;
            Q15=makeQuery(id+"F2.opExtrude","SWEPT_EDGE",EDGE,{"disambiguationData":[OSD([sQuery(id+"F0.wireOp",EDGE,"E9.4.13.0"),sQuery(id+"F0.wireOp",EDGE,"E11.13.0")])]});
            var Q16;
            Q16=makeQuery(id+"F2.opExtrude","SWEPT_EDGE",EDGE,{"disambiguationData":[OSD([sQuery(id+"F0.wireOp",EDGE,"E9.4.12.0"),sQuery(id+"F0.wireOp",EDGE,"E11.12.0")])]});
            var Q17;
            Q17=makeQuery(id+"F2.opExtrude","SWEPT_EDGE",EDGE,{"disambiguationData":[OSD([sQuery(id+"F0.wireOp",EDGE,"E9.4.11.0"),sQuery(id+"F0.wireOp",EDGE,"E11.11.0")])]});
            var Q18;
            Q18=makeQuery(id+"F2.opExtrude","SWEPT_EDGE",EDGE,{"disambiguationData":[OSD([sQuery(id+"F0.wireOp",EDGE,"E9.4.10.0"),sQuery(id+"F0.wireOp",EDGE,"E11.10.0")])]});
            var Q19;
            Q19=makeQuery(id+"F2.opExtrude","SWEPT_EDGE",EDGE,{"disambiguationData":[OSD([sQuery(id+"F0.wireOp",EDGE,"E9.4.9.0"),sQuery(id+"F0.wireOp",EDGE,"E11.9.0")])]});
            var Q20;
            Q20=makeQuery(id+"F2.opExtrude","SWEPT_EDGE",EDGE,{"disambiguationData":[OSD([sQuery(id+"F0.wireOp",EDGE,"E9.4.8.0"),sQuery(id+"F0.wireOp",EDGE,"E11.8.0")])]});
            fillet(context, id + "F3", {"entities" : qUnion([Q0, Q1, Q2, Q3, Q4, Q5, Q6, Q7, Q8, Q9, Q10, Q11, Q12, Q13, Q14, Q15, Q16, Q17, Q18, Q19, Q20]), "radius" : 1.9 * mm, "tangentPropagation" : true, "allowEdgeOverflow" : false});
        }
        {
            var Q0;
            Q0=makeQuery(id+"F2.opExtrude","SWEPT_EDGE",EDGE,{"disambiguationData":[OSD([sQuery(id+"F0.wireOp",EDGE,"E0"),sQuery(id+"F0.wireOp",EDGE,"E9.3.9.0"),sQuery(id+"F0.wireOp",EDGE,"E9.19.9.0")])]});
            var Q1;
            Q1=makeQuery(id+"F2.opExtrude","SWEPT_EDGE",EDGE,{"disambiguationData":[OSD([sQuery(id+"F0.wireOp",EDGE,"E0"),sQuery(id+"F0.wireOp",EDGE,"E9.3.8.0"),sQuery(id+"F0.wireOp",EDGE,"E9.19.8.0")])]});
            var Q2;
            Q2=makeQuery(id+"F2.opExtrude","SWEPT_EDGE",EDGE,{"disambiguationData":[OSD([sQuery(id+"F0.wireOp",EDGE,"E0"),sQuery(id+"F0.wireOp",EDGE,"E9.3.7.0"),sQuery(id+"F0.wireOp",EDGE,"E9.19.7.0")])]});
            var Q3;
            Q3=makeQuery(id+"F2.opExtrude","SWEPT_EDGE",EDGE,{"disambiguationData":[OSD([sQuery(id+"F0.wireOp",EDGE,"E0"),sQuery(id+"F0.wireOp",EDGE,"E9.3.10.0"),sQuery(id+"F0.wireOp",EDGE,"E9.19.10.0")])]});
            var Q4;
            Q4=makeQuery(id+"F2.opExtrude","SWEPT_EDGE",EDGE,{"disambiguationData":[OSD([sQuery(id+"F0.wireOp",EDGE,"E0"),sQuery(id+"F0.wireOp",EDGE,"E9.3.11.0"),sQuery(id+"F0.wireOp",EDGE,"E9.19.11.0")])]});
            var Q5;
            Q5=makeQuery(id+"F2.opExtrude","SWEPT_EDGE",EDGE,{"disambiguationData":[OSD([sQuery(id+"F0.wireOp",EDGE,"E0"),sQuery(id+"F0.wireOp",EDGE,"E9.3.12.0"),sQuery(id+"F0.wireOp",EDGE,"E9.19.12.0")])]});
            var Q6;
            Q6=makeQuery(id+"F2.opExtrude","SWEPT_EDGE",EDGE,{"disambiguationData":[OSD([sQuery(id+"F0.wireOp",EDGE,"E0"),sQuery(id+"F0.wireOp",EDGE,"E9.3.13.0"),sQuery(id+"F0.wireOp",EDGE,"E9.19.13.0")])]});
            var Q7;
            Q7=makeQuery(id+"F2.opExtrude","SWEPT_EDGE",EDGE,{"disambiguationData":[OSD([sQuery(id+"F0.wireOp",EDGE,"E0"),sQuery(id+"F0.wireOp",EDGE,"E9.3.14.0"),sQuery(id+"F0.wireOp",EDGE,"E9.19.14.0")])]});
            var Q8;
            Q8=makeQuery(id+"F2.opExtrude","SWEPT_EDGE",EDGE,{"disambiguationData":[OSD([sQuery(id+"F0.wireOp",EDGE,"E0"),sQuery(id+"F0.wireOp",EDGE,"E9.3.15.0"),sQuery(id+"F0.wireOp",EDGE,"E9.19.15.0")])]});
            var Q9;
            Q9=makeQuery(id+"F2.opExtrude","SWEPT_EDGE",EDGE,{"disambiguationData":[OSD([sQuery(id+"F0.wireOp",EDGE,"E0"),sQuery(id+"F0.wireOp",EDGE,"E9.3.6.0"),sQuery(id+"F0.wireOp",EDGE,"E9.19.6.0")])]});
            var Q10;
            Q10=makeQuery(id+"F2.opExtrude","SWEPT_EDGE",EDGE,{"disambiguationData":[OSD([sQuery(id+"F0.wireOp",EDGE,"E0"),sQuery(id+"F0.wireOp",EDGE,"E9.3.5.0"),sQuery(id+"F0.wireOp",EDGE,"E9.19.5.0")])]});
            var Q11;
            Q11=makeQuery(id+"F2.opExtrude","SWEPT_EDGE",EDGE,{"disambiguationData":[OSD([sQuery(id+"F0.wireOp",EDGE,"E0"),sQuery(id+"F0.wireOp",EDGE,"E9.3.4.0"),sQuery(id+"F0.wireOp",EDGE,"E9.19.4.0")])]});
            var Q12;
            Q12=makeQuery(id+"F2.opExtrude","SWEPT_EDGE",EDGE,{"disambiguationData":[OSD([sQuery(id+"F0.wireOp",EDGE,"E0"),sQuery(id+"F0.wireOp",EDGE,"E9.3.3.0"),sQuery(id+"F0.wireOp",EDGE,"E9.19.3.0")])]});
            var Q13;
            Q13=makeQuery(id+"F2.opExtrude","SWEPT_EDGE",EDGE,{"disambiguationData":[OSD([sQuery(id+"F0.wireOp",EDGE,"E0"),sQuery(id+"F0.wireOp",EDGE,"E8.2.0"),sQuery(id+"F0.wireOp",EDGE,"E8.2.5")])]});
            var Q14;
            Q14=makeQuery(id+"F2.opExtrude","SWEPT_EDGE",EDGE,{"disambiguationData":[OSD([sQuery(id+"F0.wireOp",EDGE,"E0"),sQuery(id+"F0.wireOp",EDGE,"E8.1.0"),sQuery(id+"F0.wireOp",EDGE,"E8.1.5")])]});
            var Q15;
            Q15=makeQuery(id+"F2.opExtrude","SWEPT_EDGE",EDGE,{"disambiguationData":[OSD([sQuery(id+"F0.wireOp",EDGE,"E0"),sQuery(id+"F0.wireOp",EDGE,"E2"),sQuery(id+"F0.wireOp",EDGE,"E5")])]});
            var Q16;
            Q16=makeQuery(id+"F2.opExtrude","SWEPT_EDGE",EDGE,{"disambiguationData":[OSD([sQuery(id+"F0.wireOp",EDGE,"E0"),sQuery(id+"F0.wireOp",EDGE,"E9.3.20.0"),sQuery(id+"F0.wireOp",EDGE,"E9.19.20.0")])]});
            var Q17;
            Q17=makeQuery(id+"F2.opExtrude","SWEPT_EDGE",EDGE,{"disambiguationData":[OSD([sQuery(id+"F0.wireOp",EDGE,"E0"),sQuery(id+"F0.wireOp",EDGE,"E9.3.19.0"),sQuery(id+"F0.wireOp",EDGE,"E9.19.19.0")])]});
            var Q18;
            Q18=makeQuery(id+"F2.opExtrude","SWEPT_EDGE",EDGE,{"disambiguationData":[OSD([sQuery(id+"F0.wireOp",EDGE,"E0"),sQuery(id+"F0.wireOp",EDGE,"E9.3.18.0"),sQuery(id+"F0.wireOp",EDGE,"E9.19.18.0")])]});
            var Q19;
            Q19=makeQuery(id+"F2.opExtrude","SWEPT_EDGE",EDGE,{"disambiguationData":[OSD([sQuery(id+"F0.wireOp",EDGE,"E0"),sQuery(id+"F0.wireOp",EDGE,"E9.3.17.0"),sQuery(id+"F0.wireOp",EDGE,"E9.19.17.0")])]});
            var Q20;
            Q20=makeQuery(id+"F2.opExtrude","SWEPT_EDGE",EDGE,{"disambiguationData":[OSD([sQuery(id+"F0.wireOp",EDGE,"E0"),sQuery(id+"F0.wireOp",EDGE,"E9.3.16.0"),sQuery(id+"F0.wireOp",EDGE,"E9.19.16.0")])]});
            fillet(context, id + "F4", {"entities" : qUnion([Q0, Q1, Q2, Q3, Q4, Q5, Q6, Q7, Q8, Q9, Q10, Q11, Q12, Q13, Q14, Q15, Q16, Q17, Q18, Q19, Q20]), "radius" : 2.8 * mm, "tangentPropagation" : true, "allowEdgeOverflow" : false});
        }
        {
            var Q0;
            Q0=makeQuery(id+"F2.opExtrude","SWEPT_EDGE",EDGE,{"disambiguationData":[OSD([sQuery(id+"F0.wireOp",EDGE,"E0"),sQuery(id+"F0.wireOp",EDGE,"E3"),sQuery(id+"F0.wireOp",EDGE,"E4")])]});
            var Q1;
            Q1=makeQuery(id+"F2.opExtrude","SWEPT_EDGE",EDGE,{"disambiguationData":[OSD([sQuery(id+"F0.wireOp",EDGE,"E0"),sQuery(id+"F0.wireOp",EDGE,"E8.1.2"),sQuery(id+"F0.wireOp",EDGE,"E8.1.3")])]});
            var Q2;
            Q2=makeQuery(id+"F2.opExtrude","SWEPT_EDGE",EDGE,{"disambiguationData":[OSD([sQuery(id+"F0.wireOp",EDGE,"E0"),sQuery(id+"F0.wireOp",EDGE,"E8.2.2"),sQuery(id+"F0.wireOp",EDGE,"E8.2.3")])]});
            var Q3;
            Q3=makeQuery(id+"F2.opExtrude","SWEPT_EDGE",EDGE,{"disambiguationData":[OSD([sQuery(id+"F0.wireOp",EDGE,"E0"),sQuery(id+"F0.wireOp",EDGE,"E9.8.3.0"),sQuery(id+"F0.wireOp",EDGE,"E9.11.3.0")])]});
            var Q4;
            Q4=makeQuery(id+"F2.opExtrude","SWEPT_EDGE",EDGE,{"disambiguationData":[OSD([sQuery(id+"F0.wireOp",EDGE,"E0"),sQuery(id+"F0.wireOp",EDGE,"E9.8.4.0"),sQuery(id+"F0.wireOp",EDGE,"E9.11.4.0")])]});
            var Q5;
            Q5=makeQuery(id+"F2.opExtrude","SWEPT_EDGE",EDGE,{"disambiguationData":[OSD([sQuery(id+"F0.wireOp",EDGE,"E0"),sQuery(id+"F0.wireOp",EDGE,"E9.8.5.0"),sQuery(id+"F0.wireOp",EDGE,"E9.11.5.0")])]});
            var Q6;
            Q6=makeQuery(id+"F2.opExtrude","SWEPT_EDGE",EDGE,{"disambiguationData":[OSD([sQuery(id+"F0.wireOp",EDGE,"E0"),sQuery(id+"F0.wireOp",EDGE,"E9.8.20.0"),sQuery(id+"F0.wireOp",EDGE,"E9.11.20.0")])]});
            var Q7;
            Q7=makeQuery(id+"F2.opExtrude","SWEPT_EDGE",EDGE,{"disambiguationData":[OSD([sQuery(id+"F0.wireOp",EDGE,"E0"),sQuery(id+"F0.wireOp",EDGE,"E9.8.19.0"),sQuery(id+"F0.wireOp",EDGE,"E9.11.19.0")])]});
            var Q8;
            Q8=makeQuery(id+"F2.opExtrude","SWEPT_EDGE",EDGE,{"disambiguationData":[OSD([sQuery(id+"F0.wireOp",EDGE,"E0"),sQuery(id+"F0.wireOp",EDGE,"E9.8.18.0"),sQuery(id+"F0.wireOp",EDGE,"E9.11.18.0")])]});
            var Q9;
            Q9=makeQuery(id+"F2.opExtrude","SWEPT_EDGE",EDGE,{"disambiguationData":[OSD([sQuery(id+"F0.wireOp",EDGE,"E0"),sQuery(id+"F0.wireOp",EDGE,"E9.8.17.0"),sQuery(id+"F0.wireOp",EDGE,"E9.11.17.0")])]});
            var Q10;
            Q10=makeQuery(id+"F2.opExtrude","SWEPT_EDGE",EDGE,{"disambiguationData":[OSD([sQuery(id+"F0.wireOp",EDGE,"E0"),sQuery(id+"F0.wireOp",EDGE,"E9.8.16.0"),sQuery(id+"F0.wireOp",EDGE,"E9.11.16.0")])]});
            var Q11;
            Q11=makeQuery(id+"F2.opExtrude","SWEPT_EDGE",EDGE,{"disambiguationData":[OSD([sQuery(id+"F0.wireOp",EDGE,"E0"),sQuery(id+"F0.wireOp",EDGE,"E9.8.6.0"),sQuery(id+"F0.wireOp",EDGE,"E9.11.6.0")])]});
            var Q12;
            Q12=makeQuery(id+"F2.opExtrude","SWEPT_EDGE",EDGE,{"disambiguationData":[OSD([sQuery(id+"F0.wireOp",EDGE,"E0"),sQuery(id+"F0.wireOp",EDGE,"E9.8.15.0"),sQuery(id+"F0.wireOp",EDGE,"E9.11.15.0")])]});
            var Q13;
            Q13=makeQuery(id+"F2.opExtrude","SWEPT_EDGE",EDGE,{"disambiguationData":[OSD([sQuery(id+"F0.wireOp",EDGE,"E0"),sQuery(id+"F0.wireOp",EDGE,"E9.8.14.0"),sQuery(id+"F0.wireOp",EDGE,"E9.11.14.0")])]});
            var Q14;
            Q14=makeQuery(id+"F2.opExtrude","SWEPT_EDGE",EDGE,{"disambiguationData":[OSD([sQuery(id+"F0.wireOp",EDGE,"E0"),sQuery(id+"F0.wireOp",EDGE,"E9.8.13.0"),sQuery(id+"F0.wireOp",EDGE,"E9.11.13.0")])]});
            var Q15;
            Q15=makeQuery(id+"F2.opExtrude","SWEPT_EDGE",EDGE,{"disambiguationData":[OSD([sQuery(id+"F0.wireOp",EDGE,"E0"),sQuery(id+"F0.wireOp",EDGE,"E9.8.7.0"),sQuery(id+"F0.wireOp",EDGE,"E9.11.7.0")])]});
            var Q16;
            Q16=makeQuery(id+"F2.opExtrude","SWEPT_EDGE",EDGE,{"disambiguationData":[OSD([sQuery(id+"F0.wireOp",EDGE,"E0"),sQuery(id+"F0.wireOp",EDGE,"E9.8.8.0"),sQuery(id+"F0.wireOp",EDGE,"E9.11.8.0")])]});
            var Q17;
            Q17=makeQuery(id+"F2.opExtrude","SWEPT_EDGE",EDGE,{"disambiguationData":[OSD([sQuery(id+"F0.wireOp",EDGE,"E0"),sQuery(id+"F0.wireOp",EDGE,"E9.8.9.0"),sQuery(id+"F0.wireOp",EDGE,"E9.11.9.0")])]});
            var Q18;
            Q18=makeQuery(id+"F2.opExtrude","SWEPT_EDGE",EDGE,{"disambiguationData":[OSD([sQuery(id+"F0.wireOp",EDGE,"E0"),sQuery(id+"F0.wireOp",EDGE,"E9.8.10.0"),sQuery(id+"F0.wireOp",EDGE,"E9.11.10.0")])]});
            var Q19;
            Q19=makeQuery(id+"F2.opExtrude","SWEPT_EDGE",EDGE,{"disambiguationData":[OSD([sQuery(id+"F0.wireOp",EDGE,"E0"),sQuery(id+"F0.wireOp",EDGE,"E9.8.11.0"),sQuery(id+"F0.wireOp",EDGE,"E9.11.11.0")])]});
            var Q20;
            Q20=makeQuery(id+"F2.opExtrude","SWEPT_EDGE",EDGE,{"disambiguationData":[OSD([sQuery(id+"F0.wireOp",EDGE,"E0"),sQuery(id+"F0.wireOp",EDGE,"E9.8.12.0"),sQuery(id+"F0.wireOp",EDGE,"E9.11.12.0")])]});
            fillet(context, id + "F5", {"entities" : qUnion([Q0, Q1, Q2, Q3, Q4, Q5, Q6, Q7, Q8, Q9, Q10, Q11, Q12, Q13, Q14, Q15, Q16, Q17, Q18, Q19, Q20]), "radius" : 2.8 * mm, "tangentPropagation" : true, "allowEdgeOverflow" : false});
        }
        {
            var Q0;
            Q0=makeQuery(id+"F2.opExtrude","SWEPT_EDGE",EDGE,{"disambiguationData":[OSD([sQuery(id+"F0.wireOp",EDGE,"E4"),sQuery(id+"F0.wireOp",EDGE,"E6")])]});
            var Q1;
            Q1=makeQuery(id+"F2.opExtrude","SWEPT_EDGE",EDGE,{"disambiguationData":[OSD([sQuery(id+"F0.wireOp",EDGE,"E8.1.1"),sQuery(id+"F0.wireOp",EDGE,"E8.1.2")])]});
            var Q2;
            Q2=makeQuery(id+"F2.opExtrude","SWEPT_EDGE",EDGE,{"disambiguationData":[OSD([sQuery(id+"F0.wireOp",EDGE,"E9.4.20.0"),sQuery(id+"F0.wireOp",EDGE,"E9.8.20.0")])]});
            var Q3;
            Q3=makeQuery(id+"F2.opExtrude","SWEPT_EDGE",EDGE,{"disambiguationData":[OSD([sQuery(id+"F0.wireOp",EDGE,"E9.4.19.0"),sQuery(id+"F0.wireOp",EDGE,"E9.8.19.0")])]});
            var Q4;
            Q4=makeQuery(id+"F2.opExtrude","SWEPT_EDGE",EDGE,{"disambiguationData":[OSD([sQuery(id+"F0.wireOp",EDGE,"E8.2.1"),sQuery(id+"F0.wireOp",EDGE,"E8.2.2")])]});
            var Q5;
            Q5=makeQuery(id+"F2.opExtrude","SWEPT_EDGE",EDGE,{"disambiguationData":[OSD([sQuery(id+"F0.wireOp",EDGE,"E9.4.3.0"),sQuery(id+"F0.wireOp",EDGE,"E9.8.3.0")])]});
            var Q6;
            Q6=makeQuery(id+"F2.opExtrude","SWEPT_EDGE",EDGE,{"disambiguationData":[OSD([sQuery(id+"F0.wireOp",EDGE,"E9.4.4.0"),sQuery(id+"F0.wireOp",EDGE,"E9.8.4.0")])]});
            var Q7;
            Q7=makeQuery(id+"F2.opExtrude","SWEPT_EDGE",EDGE,{"disambiguationData":[OSD([sQuery(id+"F0.wireOp",EDGE,"E9.4.5.0"),sQuery(id+"F0.wireOp",EDGE,"E9.8.5.0")])]});
            var Q8;
            Q8=makeQuery(id+"F2.opExtrude","SWEPT_EDGE",EDGE,{"disambiguationData":[OSD([sQuery(id+"F0.wireOp",EDGE,"E9.4.6.0"),sQuery(id+"F0.wireOp",EDGE,"E9.8.6.0")])]});
            var Q9;
            Q9=makeQuery(id+"F2.opExtrude","SWEPT_EDGE",EDGE,{"disambiguationData":[OSD([sQuery(id+"F0.wireOp",EDGE,"E9.4.18.0"),sQuery(id+"F0.wireOp",EDGE,"E9.8.18.0")])]});
            var Q10;
            Q10=makeQuery(id+"F2.opExtrude","SWEPT_EDGE",EDGE,{"disambiguationData":[OSD([sQuery(id+"F0.wireOp",EDGE,"E9.4.17.0"),sQuery(id+"F0.wireOp",EDGE,"E9.8.17.0")])]});
            var Q11;
            Q11=makeQuery(id+"F2.opExtrude","SWEPT_EDGE",EDGE,{"disambiguationData":[OSD([sQuery(id+"F0.wireOp",EDGE,"E9.4.16.0"),sQuery(id+"F0.wireOp",EDGE,"E9.8.16.0")])]});
            var Q12;
            Q12=makeQuery(id+"F2.opExtrude","SWEPT_EDGE",EDGE,{"disambiguationData":[OSD([sQuery(id+"F0.wireOp",EDGE,"E9.4.15.0"),sQuery(id+"F0.wireOp",EDGE,"E9.8.15.0")])]});
            var Q13;
            Q13=makeQuery(id+"F2.opExtrude","SWEPT_EDGE",EDGE,{"disambiguationData":[OSD([sQuery(id+"F0.wireOp",EDGE,"E9.4.14.0"),sQuery(id+"F0.wireOp",EDGE,"E9.8.14.0")])]});
            var Q14;
            Q14=makeQuery(id+"F2.opExtrude","SWEPT_EDGE",EDGE,{"disambiguationData":[OSD([sQuery(id+"F0.wireOp",EDGE,"E9.4.13.0"),sQuery(id+"F0.wireOp",EDGE,"E9.8.13.0")])]});
            var Q15;
            Q15=makeQuery(id+"F2.opExtrude","SWEPT_EDGE",EDGE,{"disambiguationData":[OSD([sQuery(id+"F0.wireOp",EDGE,"E9.4.12.0"),sQuery(id+"F0.wireOp",EDGE,"E9.8.12.0")])]});
            var Q16;
            Q16=makeQuery(id+"F2.opExtrude","SWEPT_EDGE",EDGE,{"disambiguationData":[OSD([sQuery(id+"F0.wireOp",EDGE,"E9.4.11.0"),sQuery(id+"F0.wireOp",EDGE,"E9.8.11.0")])]});
            var Q17;
            Q17=makeQuery(id+"F2.opExtrude","SWEPT_EDGE",EDGE,{"disambiguationData":[OSD([sQuery(id+"F0.wireOp",EDGE,"E9.4.10.0"),sQuery(id+"F0.wireOp",EDGE,"E9.8.10.0")])]});
            var Q18;
            Q18=makeQuery(id+"F2.opExtrude","SWEPT_EDGE",EDGE,{"disambiguationData":[OSD([sQuery(id+"F0.wireOp",EDGE,"E9.4.9.0"),sQuery(id+"F0.wireOp",EDGE,"E9.8.9.0")])]});
            var Q19;
            Q19=makeQuery(id+"F2.opExtrude","SWEPT_EDGE",EDGE,{"disambiguationData":[OSD([sQuery(id+"F0.wireOp",EDGE,"E9.4.8.0"),sQuery(id+"F0.wireOp",EDGE,"E9.8.8.0")])]});
            var Q20;
            Q20=makeQuery(id+"F2.opExtrude","SWEPT_EDGE",EDGE,{"disambiguationData":[OSD([sQuery(id+"F0.wireOp",EDGE,"E9.4.7.0"),sQuery(id+"F0.wireOp",EDGE,"E9.8.7.0")])]});
            fillet(context, id + "F6", {"entities" : qUnion([Q0, Q1, Q2, Q3, Q4, Q5, Q6, Q7, Q8, Q9, Q10, Q11, Q12, Q13, Q14, Q15, Q16, Q17, Q18, Q19, Q20]), "radius" : 3.43 * mm, "tangentPropagation" : true, "allowEdgeOverflow" : false});
        }
        {
            var Q0;
            Q0=makeQuery(id+"F1.opExtrude","SWEPT_EDGE",EDGE,{"disambiguationData":[OSD([sQuery(id+"F0.wireOp",EDGE,"E9.11.20.0"),sQuery(id+"F0.wireOp",EDGE,"E9.15.20.0")])]});
            var Q1;
            Q1=makeQuery(id+"F1.opExtrude","SWEPT_EDGE",EDGE,{"disambiguationData":[OSD([sQuery(id+"F0.wireOp",EDGE,"E9.11.19.0"),sQuery(id+"F0.wireOp",EDGE,"E9.15.19.0")])]});
            var Q2;
            Q2=makeQuery(id+"F1.opExtrude","SWEPT_EDGE",EDGE,{"disambiguationData":[OSD([sQuery(id+"F0.wireOp",EDGE,"E8.1.3"),sQuery(id+"F0.wireOp",EDGE,"E8.1.4")])]});
            var Q3;
            Q3=makeQuery(id+"F1.opExtrude","SWEPT_EDGE",EDGE,{"disambiguationData":[OSD([sQuery(id+"F0.wireOp",EDGE,"E8.2.3"),sQuery(id+"F0.wireOp",EDGE,"E8.2.4")])]});
            var Q4;
            Q4=makeQuery(id+"F1.opExtrude","SWEPT_EDGE",EDGE,{"disambiguationData":[OSD([sQuery(id+"F0.wireOp",EDGE,"E9.11.18.0"),sQuery(id+"F0.wireOp",EDGE,"E9.15.18.0")])]});
            var Q5;
            Q5=makeQuery(id+"F1.opExtrude","SWEPT_EDGE",EDGE,{"disambiguationData":[OSD([sQuery(id+"F0.wireOp",EDGE,"E9.11.3.0"),sQuery(id+"F0.wireOp",EDGE,"E9.15.3.0")])]});
            var Q6;
            Q6=makeQuery(id+"F1.opExtrude","SWEPT_EDGE",EDGE,{"disambiguationData":[OSD([sQuery(id+"F0.wireOp",EDGE,"E3"),sQuery(id+"F0.wireOp",EDGE,"E7")])]});
            var Q7;
            Q7=makeQuery(id+"F1.opExtrude","SWEPT_EDGE",EDGE,{"disambiguationData":[OSD([sQuery(id+"F0.wireOp",EDGE,"E9.11.4.0"),sQuery(id+"F0.wireOp",EDGE,"E9.15.4.0")])]});
            var Q8;
            Q8=makeQuery(id+"F1.opExtrude","SWEPT_EDGE",EDGE,{"disambiguationData":[OSD([sQuery(id+"F0.wireOp",EDGE,"E9.11.5.0"),sQuery(id+"F0.wireOp",EDGE,"E9.15.5.0")])]});
            var Q9;
            Q9=makeQuery(id+"F1.opExtrude","SWEPT_EDGE",EDGE,{"disambiguationData":[OSD([sQuery(id+"F0.wireOp",EDGE,"E9.11.6.0"),sQuery(id+"F0.wireOp",EDGE,"E9.15.6.0")])]});
            var Q10;
            Q10=makeQuery(id+"F1.opExtrude","SWEPT_EDGE",EDGE,{"disambiguationData":[OSD([sQuery(id+"F0.wireOp",EDGE,"E9.11.17.0"),sQuery(id+"F0.wireOp",EDGE,"E9.15.17.0")])]});
            var Q11;
            Q11=makeQuery(id+"F1.opExtrude","SWEPT_EDGE",EDGE,{"disambiguationData":[OSD([sQuery(id+"F0.wireOp",EDGE,"E9.11.16.0"),sQuery(id+"F0.wireOp",EDGE,"E9.15.16.0")])]});
            var Q12;
            Q12=makeQuery(id+"F1.opExtrude","SWEPT_EDGE",EDGE,{"disambiguationData":[OSD([sQuery(id+"F0.wireOp",EDGE,"E9.11.15.0"),sQuery(id+"F0.wireOp",EDGE,"E9.15.15.0")])]});
            var Q13;
            Q13=makeQuery(id+"F1.opExtrude","SWEPT_EDGE",EDGE,{"disambiguationData":[OSD([sQuery(id+"F0.wireOp",EDGE,"E9.11.14.0"),sQuery(id+"F0.wireOp",EDGE,"E9.15.14.0")])]});
            var Q14;
            Q14=makeQuery(id+"F1.opExtrude","SWEPT_EDGE",EDGE,{"disambiguationData":[OSD([sQuery(id+"F0.wireOp",EDGE,"E9.11.13.0"),sQuery(id+"F0.wireOp",EDGE,"E9.15.13.0")])]});
            var Q15;
            Q15=makeQuery(id+"F1.opExtrude","SWEPT_EDGE",EDGE,{"disambiguationData":[OSD([sQuery(id+"F0.wireOp",EDGE,"E9.11.12.0"),sQuery(id+"F0.wireOp",EDGE,"E9.15.12.0")])]});
            var Q16;
            Q16=makeQuery(id+"F1.opExtrude","SWEPT_EDGE",EDGE,{"disambiguationData":[OSD([sQuery(id+"F0.wireOp",EDGE,"E9.11.11.0"),sQuery(id+"F0.wireOp",EDGE,"E9.15.11.0")])]});
            var Q17;
            Q17=makeQuery(id+"F1.opExtrude","SWEPT_EDGE",EDGE,{"disambiguationData":[OSD([sQuery(id+"F0.wireOp",EDGE,"E9.11.10.0"),sQuery(id+"F0.wireOp",EDGE,"E9.15.10.0")])]});
            var Q18;
            Q18=makeQuery(id+"F1.opExtrude","SWEPT_EDGE",EDGE,{"disambiguationData":[OSD([sQuery(id+"F0.wireOp",EDGE,"E9.11.9.0"),sQuery(id+"F0.wireOp",EDGE,"E9.15.9.0")])]});
            var Q19;
            Q19=makeQuery(id+"F1.opExtrude","SWEPT_EDGE",EDGE,{"disambiguationData":[OSD([sQuery(id+"F0.wireOp",EDGE,"E9.11.8.0"),sQuery(id+"F0.wireOp",EDGE,"E9.15.8.0")])]});
            var Q20;
            Q20=makeQuery(id+"F1.opExtrude","SWEPT_EDGE",EDGE,{"disambiguationData":[OSD([sQuery(id+"F0.wireOp",EDGE,"E9.11.7.0"),sQuery(id+"F0.wireOp",EDGE,"E9.15.7.0")])]});
            fillet(context, id + "F7", {"entities" : qUnion([Q0, Q1, Q2, Q3, Q4, Q5, Q6, Q7, Q8, Q9, Q10, Q11, Q12, Q13, Q14, Q15, Q16, Q17, Q18, Q19, Q20]), "radius" : 1.78 * mm, "tangentPropagation" : true, "allowEdgeOverflow" : false});
        }
        {
            var Q0;
            Q0=makeQuery(id+"F1.opExtrude","SWEPT_EDGE",EDGE,{"disambiguationData":[OSD([sQuery(id+"F0.wireOp",EDGE,"E0"),sQuery(id+"F0.wireOp",EDGE,"E8.1.2"),sQuery(id+"F0.wireOp",EDGE,"E8.1.3")])]});
            var Q1;
            Q1=makeQuery(id+"F1.opExtrude","SWEPT_EDGE",EDGE,{"disambiguationData":[OSD([sQuery(id+"F0.wireOp",EDGE,"E0"),sQuery(id+"F0.wireOp",EDGE,"E3"),sQuery(id+"F0.wireOp",EDGE,"E4")])]});
            var Q2;
            Q2=makeQuery(id+"F1.opExtrude","SWEPT_EDGE",EDGE,{"disambiguationData":[OSD([sQuery(id+"F0.wireOp",EDGE,"E0"),sQuery(id+"F0.wireOp",EDGE,"E9.8.20.0"),sQuery(id+"F0.wireOp",EDGE,"E9.11.20.0")])]});
            var Q3;
            Q3=makeQuery(id+"F1.opExtrude","SWEPT_EDGE",EDGE,{"disambiguationData":[OSD([sQuery(id+"F0.wireOp",EDGE,"E0"),sQuery(id+"F0.wireOp",EDGE,"E9.8.19.0"),sQuery(id+"F0.wireOp",EDGE,"E9.11.19.0")])]});
            var Q4;
            Q4=makeQuery(id+"F1.opExtrude","SWEPT_EDGE",EDGE,{"disambiguationData":[OSD([sQuery(id+"F0.wireOp",EDGE,"E0"),sQuery(id+"F0.wireOp",EDGE,"E8.2.2"),sQuery(id+"F0.wireOp",EDGE,"E8.2.3")])]});
            var Q5;
            Q5=makeQuery(id+"F1.opExtrude","SWEPT_EDGE",EDGE,{"disambiguationData":[OSD([sQuery(id+"F0.wireOp",EDGE,"E0"),sQuery(id+"F0.wireOp",EDGE,"E9.8.3.0"),sQuery(id+"F0.wireOp",EDGE,"E9.11.3.0")])]});
            var Q6;
            Q6=makeQuery(id+"F1.opExtrude","SWEPT_EDGE",EDGE,{"disambiguationData":[OSD([sQuery(id+"F0.wireOp",EDGE,"E0"),sQuery(id+"F0.wireOp",EDGE,"E9.8.4.0"),sQuery(id+"F0.wireOp",EDGE,"E9.11.4.0")])]});
            var Q7;
            Q7=makeQuery(id+"F1.opExtrude","SWEPT_EDGE",EDGE,{"disambiguationData":[OSD([sQuery(id+"F0.wireOp",EDGE,"E0"),sQuery(id+"F0.wireOp",EDGE,"E9.8.18.0"),sQuery(id+"F0.wireOp",EDGE,"E9.11.18.0")])]});
            var Q8;
            Q8=makeQuery(id+"F1.opExtrude","SWEPT_EDGE",EDGE,{"disambiguationData":[OSD([sQuery(id+"F0.wireOp",EDGE,"E0"),sQuery(id+"F0.wireOp",EDGE,"E9.8.17.0"),sQuery(id+"F0.wireOp",EDGE,"E9.11.17.0")])]});
            var Q9;
            Q9=makeQuery(id+"F1.opExtrude","SWEPT_EDGE",EDGE,{"disambiguationData":[OSD([sQuery(id+"F0.wireOp",EDGE,"E0"),sQuery(id+"F0.wireOp",EDGE,"E9.8.16.0"),sQuery(id+"F0.wireOp",EDGE,"E9.11.16.0")])]});
            var Q10;
            Q10=makeQuery(id+"F1.opExtrude","SWEPT_EDGE",EDGE,{"disambiguationData":[OSD([sQuery(id+"F0.wireOp",EDGE,"E0"),sQuery(id+"F0.wireOp",EDGE,"E9.8.15.0"),sQuery(id+"F0.wireOp",EDGE,"E9.11.15.0")])]});
            var Q11;
            Q11=makeQuery(id+"F1.opExtrude","SWEPT_EDGE",EDGE,{"disambiguationData":[OSD([sQuery(id+"F0.wireOp",EDGE,"E0"),sQuery(id+"F0.wireOp",EDGE,"E9.8.14.0"),sQuery(id+"F0.wireOp",EDGE,"E9.11.14.0")])]});
            var Q12;
            Q12=makeQuery(id+"F1.opExtrude","SWEPT_EDGE",EDGE,{"disambiguationData":[OSD([sQuery(id+"F0.wireOp",EDGE,"E0"),sQuery(id+"F0.wireOp",EDGE,"E9.8.13.0"),sQuery(id+"F0.wireOp",EDGE,"E9.11.13.0")])]});
            var Q13;
            Q13=makeQuery(id+"F1.opExtrude","SWEPT_EDGE",EDGE,{"disambiguationData":[OSD([sQuery(id+"F0.wireOp",EDGE,"E0"),sQuery(id+"F0.wireOp",EDGE,"E9.8.5.0"),sQuery(id+"F0.wireOp",EDGE,"E9.11.5.0")])]});
            var Q14;
            Q14=makeQuery(id+"F1.opExtrude","SWEPT_EDGE",EDGE,{"disambiguationData":[OSD([sQuery(id+"F0.wireOp",EDGE,"E0"),sQuery(id+"F0.wireOp",EDGE,"E9.8.6.0"),sQuery(id+"F0.wireOp",EDGE,"E9.11.6.0")])]});
            var Q15;
            Q15=makeQuery(id+"F1.opExtrude","SWEPT_EDGE",EDGE,{"disambiguationData":[OSD([sQuery(id+"F0.wireOp",EDGE,"E0"),sQuery(id+"F0.wireOp",EDGE,"E9.8.7.0"),sQuery(id+"F0.wireOp",EDGE,"E9.11.7.0")])]});
            var Q16;
            Q16=makeQuery(id+"F1.opExtrude","SWEPT_EDGE",EDGE,{"disambiguationData":[OSD([sQuery(id+"F0.wireOp",EDGE,"E0"),sQuery(id+"F0.wireOp",EDGE,"E9.8.11.0"),sQuery(id+"F0.wireOp",EDGE,"E9.11.11.0")])]});
            var Q17;
            Q17=makeQuery(id+"F1.opExtrude","SWEPT_EDGE",EDGE,{"disambiguationData":[OSD([sQuery(id+"F0.wireOp",EDGE,"E0"),sQuery(id+"F0.wireOp",EDGE,"E9.8.10.0"),sQuery(id+"F0.wireOp",EDGE,"E9.11.10.0")])]});
            var Q18;
            Q18=makeQuery(id+"F1.opExtrude","SWEPT_EDGE",EDGE,{"disambiguationData":[OSD([sQuery(id+"F0.wireOp",EDGE,"E0"),sQuery(id+"F0.wireOp",EDGE,"E9.8.9.0"),sQuery(id+"F0.wireOp",EDGE,"E9.11.9.0")])]});
            var Q19;
            Q19=makeQuery(id+"F1.opExtrude","SWEPT_EDGE",EDGE,{"disambiguationData":[OSD([sQuery(id+"F0.wireOp",EDGE,"E0"),sQuery(id+"F0.wireOp",EDGE,"E9.8.8.0"),sQuery(id+"F0.wireOp",EDGE,"E9.11.8.0")])]});
            var Q20;
            Q20=makeQuery(id+"F1.opExtrude","SWEPT_EDGE",EDGE,{"disambiguationData":[OSD([sQuery(id+"F0.wireOp",EDGE,"E0"),sQuery(id+"F0.wireOp",EDGE,"E9.8.12.0"),sQuery(id+"F0.wireOp",EDGE,"E9.11.12.0")])]});
            fillet(context, id + "F8", {"entities" : qUnion([Q0, Q1, Q2, Q3, Q4, Q5, Q6, Q7, Q8, Q9, Q10, Q11, Q12, Q13, Q14, Q15, Q16, Q17, Q18, Q19, Q20]), "radius" : 2.1 * mm, "tangentPropagation" : true, "allowEdgeOverflow" : false});
        }
        {
            var Q0;
            Q0=makeQuery(id+"F1.opExtrude","SWEPT_EDGE",EDGE,{"disambiguationData":[OSD([sQuery(id+"F0.wireOp",EDGE,"E0"),sQuery(id+"F0.wireOp",EDGE,"E2"),sQuery(id+"F0.wireOp",EDGE,"E5")])]});
            var Q1;
            Q1=makeQuery(id+"F1.opExtrude","SWEPT_EDGE",EDGE,{"disambiguationData":[OSD([sQuery(id+"F0.wireOp",EDGE,"E0"),sQuery(id+"F0.wireOp",EDGE,"E9.3.20.0"),sQuery(id+"F0.wireOp",EDGE,"E9.19.20.0")])]});
            var Q2;
            Q2=makeQuery(id+"F1.opExtrude","SWEPT_EDGE",EDGE,{"disambiguationData":[OSD([sQuery(id+"F0.wireOp",EDGE,"E0"),sQuery(id+"F0.wireOp",EDGE,"E8.1.0"),sQuery(id+"F0.wireOp",EDGE,"E8.1.5")])]});
            var Q3;
            Q3=makeQuery(id+"F1.opExtrude","SWEPT_EDGE",EDGE,{"disambiguationData":[OSD([sQuery(id+"F0.wireOp",EDGE,"E0"),sQuery(id+"F0.wireOp",EDGE,"E8.2.0"),sQuery(id+"F0.wireOp",EDGE,"E8.2.5")])]});
            var Q4;
            Q4=makeQuery(id+"F1.opExtrude","SWEPT_EDGE",EDGE,{"disambiguationData":[OSD([sQuery(id+"F0.wireOp",EDGE,"E0"),sQuery(id+"F0.wireOp",EDGE,"E9.3.3.0"),sQuery(id+"F0.wireOp",EDGE,"E9.19.3.0")])]});
            var Q5;
            Q5=makeQuery(id+"F1.opExtrude","SWEPT_EDGE",EDGE,{"disambiguationData":[OSD([sQuery(id+"F0.wireOp",EDGE,"E0"),sQuery(id+"F0.wireOp",EDGE,"E9.3.4.0"),sQuery(id+"F0.wireOp",EDGE,"E9.19.4.0")])]});
            var Q6;
            Q6=makeQuery(id+"F1.opExtrude","SWEPT_EDGE",EDGE,{"disambiguationData":[OSD([sQuery(id+"F0.wireOp",EDGE,"E0"),sQuery(id+"F0.wireOp",EDGE,"E9.3.19.0"),sQuery(id+"F0.wireOp",EDGE,"E9.19.19.0")])]});
            var Q7;
            Q7=makeQuery(id+"F1.opExtrude","SWEPT_EDGE",EDGE,{"disambiguationData":[OSD([sQuery(id+"F0.wireOp",EDGE,"E0"),sQuery(id+"F0.wireOp",EDGE,"E9.3.18.0"),sQuery(id+"F0.wireOp",EDGE,"E9.19.18.0")])]});
            var Q8;
            Q8=makeQuery(id+"F1.opExtrude","SWEPT_EDGE",EDGE,{"disambiguationData":[OSD([sQuery(id+"F0.wireOp",EDGE,"E0"),sQuery(id+"F0.wireOp",EDGE,"E9.3.17.0"),sQuery(id+"F0.wireOp",EDGE,"E9.19.17.0")])]});
            var Q9;
            Q9=makeQuery(id+"F1.opExtrude","SWEPT_EDGE",EDGE,{"disambiguationData":[OSD([sQuery(id+"F0.wireOp",EDGE,"E0"),sQuery(id+"F0.wireOp",EDGE,"E9.3.16.0"),sQuery(id+"F0.wireOp",EDGE,"E9.19.16.0")])]});
            var Q10;
            Q10=makeQuery(id+"F1.opExtrude","SWEPT_EDGE",EDGE,{"disambiguationData":[OSD([sQuery(id+"F0.wireOp",EDGE,"E0"),sQuery(id+"F0.wireOp",EDGE,"E9.3.15.0"),sQuery(id+"F0.wireOp",EDGE,"E9.19.15.0")])]});
            var Q11;
            Q11=makeQuery(id+"F1.opExtrude","SWEPT_EDGE",EDGE,{"disambiguationData":[OSD([sQuery(id+"F0.wireOp",EDGE,"E0"),sQuery(id+"F0.wireOp",EDGE,"E9.3.14.0"),sQuery(id+"F0.wireOp",EDGE,"E9.19.14.0")])]});
            var Q12;
            Q12=makeQuery(id+"F1.opExtrude","SWEPT_EDGE",EDGE,{"disambiguationData":[OSD([sQuery(id+"F0.wireOp",EDGE,"E0"),sQuery(id+"F0.wireOp",EDGE,"E9.3.5.0"),sQuery(id+"F0.wireOp",EDGE,"E9.19.5.0")])]});
            var Q13;
            Q13=makeQuery(id+"F1.opExtrude","SWEPT_EDGE",EDGE,{"disambiguationData":[OSD([sQuery(id+"F0.wireOp",EDGE,"E0"),sQuery(id+"F0.wireOp",EDGE,"E9.3.6.0"),sQuery(id+"F0.wireOp",EDGE,"E9.19.6.0")])]});
            var Q14;
            Q14=makeQuery(id+"F1.opExtrude","SWEPT_EDGE",EDGE,{"disambiguationData":[OSD([sQuery(id+"F0.wireOp",EDGE,"E0"),sQuery(id+"F0.wireOp",EDGE,"E9.3.13.0"),sQuery(id+"F0.wireOp",EDGE,"E9.19.13.0")])]});
            var Q15;
            Q15=makeQuery(id+"F1.opExtrude","SWEPT_EDGE",EDGE,{"disambiguationData":[OSD([sQuery(id+"F0.wireOp",EDGE,"E0"),sQuery(id+"F0.wireOp",EDGE,"E9.3.12.0"),sQuery(id+"F0.wireOp",EDGE,"E9.19.12.0")])]});
            var Q16;
            Q16=makeQuery(id+"F1.opExtrude","SWEPT_EDGE",EDGE,{"disambiguationData":[OSD([sQuery(id+"F0.wireOp",EDGE,"E0"),sQuery(id+"F0.wireOp",EDGE,"E9.3.11.0"),sQuery(id+"F0.wireOp",EDGE,"E9.19.11.0")])]});
            var Q17;
            Q17=makeQuery(id+"F1.opExtrude","SWEPT_EDGE",EDGE,{"disambiguationData":[OSD([sQuery(id+"F0.wireOp",EDGE,"E0"),sQuery(id+"F0.wireOp",EDGE,"E9.3.10.0"),sQuery(id+"F0.wireOp",EDGE,"E9.19.10.0")])]});
            var Q18;
            Q18=makeQuery(id+"F1.opExtrude","SWEPT_EDGE",EDGE,{"disambiguationData":[OSD([sQuery(id+"F0.wireOp",EDGE,"E0"),sQuery(id+"F0.wireOp",EDGE,"E9.3.9.0"),sQuery(id+"F0.wireOp",EDGE,"E9.19.9.0")])]});
            var Q19;
            Q19=makeQuery(id+"F1.opExtrude","SWEPT_EDGE",EDGE,{"disambiguationData":[OSD([sQuery(id+"F0.wireOp",EDGE,"E0"),sQuery(id+"F0.wireOp",EDGE,"E9.3.8.0"),sQuery(id+"F0.wireOp",EDGE,"E9.19.8.0")])]});
            var Q20;
            Q20=makeQuery(id+"F1.opExtrude","SWEPT_EDGE",EDGE,{"disambiguationData":[OSD([sQuery(id+"F0.wireOp",EDGE,"E0"),sQuery(id+"F0.wireOp",EDGE,"E9.3.7.0"),sQuery(id+"F0.wireOp",EDGE,"E9.19.7.0")])]});
            fillet(context, id + "F9", {"entities" : qUnion([Q0, Q1, Q2, Q3, Q4, Q5, Q6, Q7, Q8, Q9, Q10, Q11, Q12, Q13, Q14, Q15, Q16, Q17, Q18, Q19, Q20]), "radius" : 2.07 * mm, "tangentPropagation" : true, "allowEdgeOverflow" : false});
        }
        {
            var Q0;
            Q0=makeQuery(id+"F1.opExtrude","SWEPT_EDGE",EDGE,{"disambiguationData":[OSD([sQuery(id+"F0.wireOp",EDGE,"E8.1.4"),sQuery(id+"F0.wireOp",EDGE,"E8.1.5")])]});
            var Q1;
            Q1=makeQuery(id+"F1.opExtrude","SWEPT_EDGE",EDGE,{"disambiguationData":[OSD([sQuery(id+"F0.wireOp",EDGE,"E8.2.4"),sQuery(id+"F0.wireOp",EDGE,"E8.2.5")])]});
            var Q2;
            Q2=makeQuery(id+"F1.opExtrude","SWEPT_EDGE",EDGE,{"disambiguationData":[OSD([sQuery(id+"F0.wireOp",EDGE,"E9.15.3.0"),sQuery(id+"F0.wireOp",EDGE,"E9.19.3.0")])]});
            var Q3;
            Q3=makeQuery(id+"F1.opExtrude","SWEPT_EDGE",EDGE,{"disambiguationData":[OSD([sQuery(id+"F0.wireOp",EDGE,"E9.15.4.0"),sQuery(id+"F0.wireOp",EDGE,"E9.19.4.0")])]});
            var Q4;
            Q4=makeQuery(id+"F1.opExtrude","SWEPT_EDGE",EDGE,{"disambiguationData":[OSD([sQuery(id+"F0.wireOp",EDGE,"E5"),sQuery(id+"F0.wireOp",EDGE,"E7")])]});
            var Q5;
            Q5=makeQuery(id+"F1.opExtrude","SWEPT_EDGE",EDGE,{"disambiguationData":[OSD([sQuery(id+"F0.wireOp",EDGE,"E9.15.20.0"),sQuery(id+"F0.wireOp",EDGE,"E9.19.20.0")])]});
            var Q6;
            Q6=makeQuery(id+"F1.opExtrude","SWEPT_EDGE",EDGE,{"disambiguationData":[OSD([sQuery(id+"F0.wireOp",EDGE,"E9.15.19.0"),sQuery(id+"F0.wireOp",EDGE,"E9.19.19.0")])]});
            var Q7;
            Q7=makeQuery(id+"F1.opExtrude","SWEPT_EDGE",EDGE,{"disambiguationData":[OSD([sQuery(id+"F0.wireOp",EDGE,"E9.15.18.0"),sQuery(id+"F0.wireOp",EDGE,"E9.19.18.0")])]});
            var Q8;
            Q8=makeQuery(id+"F1.opExtrude","SWEPT_EDGE",EDGE,{"disambiguationData":[OSD([sQuery(id+"F0.wireOp",EDGE,"E9.15.17.0"),sQuery(id+"F0.wireOp",EDGE,"E9.19.17.0")])]});
            var Q9;
            Q9=makeQuery(id+"F1.opExtrude","SWEPT_EDGE",EDGE,{"disambiguationData":[OSD([sQuery(id+"F0.wireOp",EDGE,"E9.15.16.0"),sQuery(id+"F0.wireOp",EDGE,"E9.19.16.0")])]});
            var Q10;
            Q10=makeQuery(id+"F1.opExtrude","SWEPT_EDGE",EDGE,{"disambiguationData":[OSD([sQuery(id+"F0.wireOp",EDGE,"E9.15.15.0"),sQuery(id+"F0.wireOp",EDGE,"E9.19.15.0")])]});
            var Q11;
            Q11=makeQuery(id+"F1.opExtrude","SWEPT_EDGE",EDGE,{"disambiguationData":[OSD([sQuery(id+"F0.wireOp",EDGE,"E9.15.14.0"),sQuery(id+"F0.wireOp",EDGE,"E9.19.14.0")])]});
            var Q12;
            Q12=makeQuery(id+"F1.opExtrude","SWEPT_EDGE",EDGE,{"disambiguationData":[OSD([sQuery(id+"F0.wireOp",EDGE,"E9.15.13.0"),sQuery(id+"F0.wireOp",EDGE,"E9.19.13.0")])]});
            var Q13;
            Q13=makeQuery(id+"F1.opExtrude","SWEPT_EDGE",EDGE,{"disambiguationData":[OSD([sQuery(id+"F0.wireOp",EDGE,"E9.15.12.0"),sQuery(id+"F0.wireOp",EDGE,"E9.19.12.0")])]});
            var Q14;
            Q14=makeQuery(id+"F1.opExtrude","SWEPT_EDGE",EDGE,{"disambiguationData":[OSD([sQuery(id+"F0.wireOp",EDGE,"E9.15.11.0"),sQuery(id+"F0.wireOp",EDGE,"E9.19.11.0")])]});
            var Q15;
            Q15=makeQuery(id+"F1.opExtrude","SWEPT_EDGE",EDGE,{"disambiguationData":[OSD([sQuery(id+"F0.wireOp",EDGE,"E9.15.10.0"),sQuery(id+"F0.wireOp",EDGE,"E9.19.10.0")])]});
            var Q16;
            Q16=makeQuery(id+"F1.opExtrude","SWEPT_EDGE",EDGE,{"disambiguationData":[OSD([sQuery(id+"F0.wireOp",EDGE,"E9.15.9.0"),sQuery(id+"F0.wireOp",EDGE,"E9.19.9.0")])]});
            var Q17;
            Q17=makeQuery(id+"F1.opExtrude","SWEPT_EDGE",EDGE,{"disambiguationData":[OSD([sQuery(id+"F0.wireOp",EDGE,"E9.15.8.0"),sQuery(id+"F0.wireOp",EDGE,"E9.19.8.0")])]});
            var Q18;
            Q18=makeQuery(id+"F1.opExtrude","SWEPT_EDGE",EDGE,{"disambiguationData":[OSD([sQuery(id+"F0.wireOp",EDGE,"E9.15.7.0"),sQuery(id+"F0.wireOp",EDGE,"E9.19.7.0")])]});
            var Q19;
            Q19=makeQuery(id+"F1.opExtrude","SWEPT_EDGE",EDGE,{"disambiguationData":[OSD([sQuery(id+"F0.wireOp",EDGE,"E9.15.6.0"),sQuery(id+"F0.wireOp",EDGE,"E9.19.6.0")])]});
            var Q20;
            Q20=makeQuery(id+"F1.opExtrude","SWEPT_EDGE",EDGE,{"disambiguationData":[OSD([sQuery(id+"F0.wireOp",EDGE,"E9.15.5.0"),sQuery(id+"F0.wireOp",EDGE,"E9.19.5.0")])]});
            fillet(context, id + "F10", {"entities" : qUnion([Q0, Q1, Q2, Q3, Q4, Q5, Q6, Q7, Q8, Q9, Q10, Q11, Q12, Q13, Q14, Q15, Q16, Q17, Q18, Q19, Q20]), "radius" : 3.17 * mm, "tangentPropagation" : true, "allowEdgeOverflow" : false});
        }
        {
            var Q0;
            Q0=makeQuery(id+"F1.opExtrude","SWEPT_BODY",BODY,{"disambiguationData":[OSD([sQuery(id+"F0.wireOp",EDGE,"E0"),sQuery(id+"F0.wireOp",EDGE,"E1"),sQuery(id+"F0.wireOp",EDGE,"E3"),sQuery(id+"F0.wireOp",EDGE,"E5"),sQuery(id+"F0.wireOp",EDGE,"E7"),sQuery(id+"F0.wireOp",EDGE,"E8.1.3"),sQuery(id+"F0.wireOp",EDGE,"E8.1.4"),sQuery(id+"F0.wireOp",EDGE,"E8.1.5"),sQuery(id+"F0.wireOp",EDGE,"E8.2.3"),sQuery(id+"F0.wireOp",EDGE,"E8.2.4"),sQuery(id+"F0.wireOp",EDGE,"E8.2.5"),sQuery(id+"F0.wireOp",EDGE,"E9.11.3.0"),sQuery(id+"F0.wireOp",EDGE,"E9.15.3.0"),sQuery(id+"F0.wireOp",EDGE,"E9.19.3.0"),sQuery(id+"F0.wireOp",EDGE,"E9.11.4.0"),sQuery(id+"F0.wireOp",EDGE,"E9.15.4.0"),sQuery(id+"F0.wireOp",EDGE,"E9.19.4.0"),sQuery(id+"F0.wireOp",EDGE,"E9.11.5.0"),sQuery(id+"F0.wireOp",EDGE,"E9.15.5.0"),sQuery(id+"F0.wireOp",EDGE,"E9.19.5.0"),sQuery(id+"F0.wireOp",EDGE,"E9.11.6.0"),sQuery(id+"F0.wireOp",EDGE,"E9.15.6.0"),sQuery(id+"F0.wireOp",EDGE,"E9.19.6.0"),sQuery(id+"F0.wireOp",EDGE,"E9.11.7.0"),sQuery(id+"F0.wireOp",EDGE,"E9.15.7.0"),sQuery(id+"F0.wireOp",EDGE,"E9.19.7.0"),sQuery(id+"F0.wireOp",EDGE,"E9.11.8.0"),sQuery(id+"F0.wireOp",EDGE,"E9.15.8.0"),sQuery(id+"F0.wireOp",EDGE,"E9.19.8.0"),sQuery(id+"F0.wireOp",EDGE,"E9.11.9.0"),sQuery(id+"F0.wireOp",EDGE,"E9.15.9.0"),sQuery(id+"F0.wireOp",EDGE,"E9.19.9.0"),sQuery(id+"F0.wireOp",EDGE,"E9.11.10.0"),sQuery(id+"F0.wireOp",EDGE,"E9.15.10.0"),sQuery(id+"F0.wireOp",EDGE,"E9.19.10.0"),sQuery(id+"F0.wireOp",EDGE,"E9.11.11.0"),sQuery(id+"F0.wireOp",EDGE,"E9.15.11.0"),sQuery(id+"F0.wireOp",EDGE,"E9.19.11.0"),sQuery(id+"F0.wireOp",EDGE,"E9.11.12.0"),sQuery(id+"F0.wireOp",EDGE,"E9.15.12.0"),sQuery(id+"F0.wireOp",EDGE,"E9.19.12.0"),sQuery(id+"F0.wireOp",EDGE,"E9.11.13.0"),sQuery(id+"F0.wireOp",EDGE,"E9.15.13.0"),sQuery(id+"F0.wireOp",EDGE,"E9.19.13.0"),sQuery(id+"F0.wireOp",EDGE,"E9.11.14.0"),sQuery(id+"F0.wireOp",EDGE,"E9.15.14.0"),sQuery(id+"F0.wireOp",EDGE,"E9.19.14.0"),sQuery(id+"F0.wireOp",EDGE,"E9.11.15.0"),sQuery(id+"F0.wireOp",EDGE,"E9.15.15.0"),sQuery(id+"F0.wireOp",EDGE,"E9.19.15.0"),sQuery(id+"F0.wireOp",EDGE,"E9.11.16.0"),sQuery(id+"F0.wireOp",EDGE,"E9.15.16.0"),sQuery(id+"F0.wireOp",EDGE,"E9.19.16.0"),sQuery(id+"F0.wireOp",EDGE,"E9.11.17.0"),sQuery(id+"F0.wireOp",EDGE,"E9.15.17.0"),sQuery(id+"F0.wireOp",EDGE,"E9.19.17.0"),sQuery(id+"F0.wireOp",EDGE,"E9.11.18.0"),sQuery(id+"F0.wireOp",EDGE,"E9.15.18.0"),sQuery(id+"F0.wireOp",EDGE,"E9.19.18.0"),sQuery(id+"F0.wireOp",EDGE,"E9.11.19.0"),sQuery(id+"F0.wireOp",EDGE,"E9.15.19.0"),sQuery(id+"F0.wireOp",EDGE,"E9.19.19.0"),sQuery(id+"F0.wireOp",EDGE,"E9.11.20.0"),sQuery(id+"F0.wireOp",EDGE,"E9.15.20.0"),sQuery(id+"F0.wireOp",EDGE,"E9.19.20.0")])]});
            var Q1;
            Q1=makeQuery(id+"F1.opExtrude","CAP_EDGE",EDGE,{"disambiguationData":[OSD([sQuery(id+"F0.wireOp",EDGE,"E1")])],"isStart":false});
            transform(context, id + "F11", {"entities" : qUnion([Q0]), "transformType" : TransformType.ROTATION, "transformAxis" : qUnion([Q1]), "angle" : 8.65 * degree, "makeCopy" : false});
        }
        {
            var Q0;
            Q0=makeQuery(id+"F1.opExtrude","SWEPT_BODY",BODY,{"disambiguationData":[OSD([sQuery(id+"F0.wireOp",EDGE,"E0"),sQuery(id+"F0.wireOp",EDGE,"E1"),sQuery(id+"F0.wireOp",EDGE,"E3"),sQuery(id+"F0.wireOp",EDGE,"E5"),sQuery(id+"F0.wireOp",EDGE,"E7"),sQuery(id+"F0.wireOp",EDGE,"E8.1.3"),sQuery(id+"F0.wireOp",EDGE,"E8.1.4"),sQuery(id+"F0.wireOp",EDGE,"E8.1.5"),sQuery(id+"F0.wireOp",EDGE,"E8.2.3"),sQuery(id+"F0.wireOp",EDGE,"E8.2.4"),sQuery(id+"F0.wireOp",EDGE,"E8.2.5"),sQuery(id+"F0.wireOp",EDGE,"E9.11.3.0"),sQuery(id+"F0.wireOp",EDGE,"E9.15.3.0"),sQuery(id+"F0.wireOp",EDGE,"E9.19.3.0"),sQuery(id+"F0.wireOp",EDGE,"E9.11.4.0"),sQuery(id+"F0.wireOp",EDGE,"E9.15.4.0"),sQuery(id+"F0.wireOp",EDGE,"E9.19.4.0"),sQuery(id+"F0.wireOp",EDGE,"E9.11.5.0"),sQuery(id+"F0.wireOp",EDGE,"E9.15.5.0"),sQuery(id+"F0.wireOp",EDGE,"E9.19.5.0"),sQuery(id+"F0.wireOp",EDGE,"E9.11.6.0"),sQuery(id+"F0.wireOp",EDGE,"E9.15.6.0"),sQuery(id+"F0.wireOp",EDGE,"E9.19.6.0"),sQuery(id+"F0.wireOp",EDGE,"E9.11.7.0"),sQuery(id+"F0.wireOp",EDGE,"E9.15.7.0"),sQuery(id+"F0.wireOp",EDGE,"E9.19.7.0"),sQuery(id+"F0.wireOp",EDGE,"E9.11.8.0"),sQuery(id+"F0.wireOp",EDGE,"E9.15.8.0"),sQuery(id+"F0.wireOp",EDGE,"E9.19.8.0"),sQuery(id+"F0.wireOp",EDGE,"E9.11.9.0"),sQuery(id+"F0.wireOp",EDGE,"E9.15.9.0"),sQuery(id+"F0.wireOp",EDGE,"E9.19.9.0"),sQuery(id+"F0.wireOp",EDGE,"E9.11.10.0"),sQuery(id+"F0.wireOp",EDGE,"E9.15.10.0"),sQuery(id+"F0.wireOp",EDGE,"E9.19.10.0"),sQuery(id+"F0.wireOp",EDGE,"E9.11.11.0"),sQuery(id+"F0.wireOp",EDGE,"E9.15.11.0"),sQuery(id+"F0.wireOp",EDGE,"E9.19.11.0"),sQuery(id+"F0.wireOp",EDGE,"E9.11.12.0"),sQuery(id+"F0.wireOp",EDGE,"E9.15.12.0"),sQuery(id+"F0.wireOp",EDGE,"E9.19.12.0"),sQuery(id+"F0.wireOp",EDGE,"E9.11.13.0"),sQuery(id+"F0.wireOp",EDGE,"E9.15.13.0"),sQuery(id+"F0.wireOp",EDGE,"E9.19.13.0"),sQuery(id+"F0.wireOp",EDGE,"E9.11.14.0"),sQuery(id+"F0.wireOp",EDGE,"E9.15.14.0"),sQuery(id+"F0.wireOp",EDGE,"E9.19.14.0"),sQuery(id+"F0.wireOp",EDGE,"E9.11.15.0"),sQuery(id+"F0.wireOp",EDGE,"E9.15.15.0"),sQuery(id+"F0.wireOp",EDGE,"E9.19.15.0"),sQuery(id+"F0.wireOp",EDGE,"E9.11.16.0"),sQuery(id+"F0.wireOp",EDGE,"E9.15.16.0"),sQuery(id+"F0.wireOp",EDGE,"E9.19.16.0"),sQuery(id+"F0.wireOp",EDGE,"E9.11.17.0"),sQuery(id+"F0.wireOp",EDGE,"E9.15.17.0"),sQuery(id+"F0.wireOp",EDGE,"E9.19.17.0"),sQuery(id+"F0.wireOp",EDGE,"E9.11.18.0"),sQuery(id+"F0.wireOp",EDGE,"E9.15.18.0"),sQuery(id+"F0.wireOp",EDGE,"E9.19.18.0"),sQuery(id+"F0.wireOp",EDGE,"E9.11.19.0"),sQuery(id+"F0.wireOp",EDGE,"E9.15.19.0"),sQuery(id+"F0.wireOp",EDGE,"E9.19.19.0"),sQuery(id+"F0.wireOp",EDGE,"E9.11.20.0"),sQuery(id+"F0.wireOp",EDGE,"E9.15.20.0"),sQuery(id+"F0.wireOp",EDGE,"E9.19.20.0")])]});
            transform(context, id + "F12", {"entities" : qUnion([Q0]), "transformType" : TransformType.TRANSLATION_3D, "dx" : 0 * mm, "dy" : 0 * mm, "dz" : -63.5 * mm, "makeCopy" : false});
        }
        {
            var Q0;
            Q0=makeQuery(id+"F2.opExtrude","SWEPT_BODY",BODY,{"disambiguationData":[OSD([sQuery(id+"F0.wireOp",EDGE,"E0"),sQuery(id+"F0.wireOp",EDGE,"E1"),sQuery(id+"F0.wireOp",EDGE,"E2"),sQuery(id+"F0.wireOp",EDGE,"E4"),sQuery(id+"F0.wireOp",EDGE,"E6"),sQuery(id+"F0.wireOp",EDGE,"E8.1.0"),sQuery(id+"F0.wireOp",EDGE,"E8.1.1"),sQuery(id+"F0.wireOp",EDGE,"E8.1.2"),sQuery(id+"F0.wireOp",EDGE,"E8.2.0"),sQuery(id+"F0.wireOp",EDGE,"E8.2.1"),sQuery(id+"F0.wireOp",EDGE,"E8.2.2"),sQuery(id+"F0.wireOp",EDGE,"E9.3.3.0"),sQuery(id+"F0.wireOp",EDGE,"E9.4.3.0"),sQuery(id+"F0.wireOp",EDGE,"E9.8.3.0"),sQuery(id+"F0.wireOp",EDGE,"E9.3.4.0"),sQuery(id+"F0.wireOp",EDGE,"E9.4.4.0"),sQuery(id+"F0.wireOp",EDGE,"E9.8.4.0"),sQuery(id+"F0.wireOp",EDGE,"E9.3.5.0"),sQuery(id+"F0.wireOp",EDGE,"E9.4.5.0"),sQuery(id+"F0.wireOp",EDGE,"E9.8.5.0"),sQuery(id+"F0.wireOp",EDGE,"E9.3.6.0"),sQuery(id+"F0.wireOp",EDGE,"E9.4.6.0"),sQuery(id+"F0.wireOp",EDGE,"E9.8.6.0"),sQuery(id+"F0.wireOp",EDGE,"E9.3.7.0"),sQuery(id+"F0.wireOp",EDGE,"E9.4.7.0"),sQuery(id+"F0.wireOp",EDGE,"E9.8.7.0"),sQuery(id+"F0.wireOp",EDGE,"E9.3.8.0"),sQuery(id+"F0.wireOp",EDGE,"E9.4.8.0"),sQuery(id+"F0.wireOp",EDGE,"E9.8.8.0"),sQuery(id+"F0.wireOp",EDGE,"E9.3.9.0"),sQuery(id+"F0.wireOp",EDGE,"E9.4.9.0"),sQuery(id+"F0.wireOp",EDGE,"E9.8.9.0"),sQuery(id+"F0.wireOp",EDGE,"E9.3.10.0"),sQuery(id+"F0.wireOp",EDGE,"E9.4.10.0"),sQuery(id+"F0.wireOp",EDGE,"E9.8.10.0"),sQuery(id+"F0.wireOp",EDGE,"E9.3.11.0"),sQuery(id+"F0.wireOp",EDGE,"E9.4.11.0"),sQuery(id+"F0.wireOp",EDGE,"E9.8.11.0"),sQuery(id+"F0.wireOp",EDGE,"E9.3.12.0"),sQuery(id+"F0.wireOp",EDGE,"E9.4.12.0"),sQuery(id+"F0.wireOp",EDGE,"E9.8.12.0"),sQuery(id+"F0.wireOp",EDGE,"E9.3.13.0"),sQuery(id+"F0.wireOp",EDGE,"E9.4.13.0"),sQuery(id+"F0.wireOp",EDGE,"E9.8.13.0"),sQuery(id+"F0.wireOp",EDGE,"E9.3.14.0"),sQuery(id+"F0.wireOp",EDGE,"E9.4.14.0"),sQuery(id+"F0.wireOp",EDGE,"E9.8.14.0"),sQuery(id+"F0.wireOp",EDGE,"E9.3.15.0"),sQuery(id+"F0.wireOp",EDGE,"E9.4.15.0"),sQuery(id+"F0.wireOp",EDGE,"E9.8.15.0"),sQuery(id+"F0.wireOp",EDGE,"E9.3.16.0"),sQuery(id+"F0.wireOp",EDGE,"E9.4.16.0"),sQuery(id+"F0.wireOp",EDGE,"E9.8.16.0"),sQuery(id+"F0.wireOp",EDGE,"E9.3.17.0"),sQuery(id+"F0.wireOp",EDGE,"E9.4.17.0"),sQuery(id+"F0.wireOp",EDGE,"E9.8.17.0"),sQuery(id+"F0.wireOp",EDGE,"E9.3.18.0"),sQuery(id+"F0.wireOp",EDGE,"E9.4.18.0"),sQuery(id+"F0.wireOp",EDGE,"E9.8.18.0"),sQuery(id+"F0.wireOp",EDGE,"E9.3.19.0"),sQuery(id+"F0.wireOp",EDGE,"E9.4.19.0"),sQuery(id+"F0.wireOp",EDGE,"E9.8.19.0"),sQuery(id+"F0.wireOp",EDGE,"E9.3.20.0"),sQuery(id+"F0.wireOp",EDGE,"E9.4.20.0"),sQuery(id+"F0.wireOp",EDGE,"E9.8.20.0"),sQuery(id+"F0.wireOp",EDGE,"E10"),sQuery(id+"F0.wireOp",EDGE,"E11.1.0"),sQuery(id+"F0.wireOp",EDGE,"E11.2.0"),sQuery(id+"F0.wireOp",EDGE,"E11.3.0"),sQuery(id+"F0.wireOp",EDGE,"E11.4.0"),sQuery(id+"F0.wireOp",EDGE,"E11.5.0"),sQuery(id+"F0.wireOp",EDGE,"E11.6.0"),sQuery(id+"F0.wireOp",EDGE,"E11.7.0"),sQuery(id+"F0.wireOp",EDGE,"E11.8.0"),sQuery(id+"F0.wireOp",EDGE,"E11.9.0"),sQuery(id+"F0.wireOp",EDGE,"E11.10.0"),sQuery(id+"F0.wireOp",EDGE,"E11.11.0"),sQuery(id+"F0.wireOp",EDGE,"E11.12.0"),sQuery(id+"F0.wireOp",EDGE,"E11.13.0"),sQuery(id+"F0.wireOp",EDGE,"E11.14.0"),sQuery(id+"F0.wireOp",EDGE,"E11.15.0"),sQuery(id+"F0.wireOp",EDGE,"E11.16.0"),sQuery(id+"F0.wireOp",EDGE,"E11.17.0"),sQuery(id+"F0.wireOp",EDGE,"E11.18.0"),sQuery(id+"F0.wireOp",EDGE,"E11.19.0"),sQuery(id+"F0.wireOp",EDGE,"E11.20.0")])]});
            var Q1;
            Q1=makeQuery(id+"F1.opExtrude","SWEPT_BODY",BODY,{"disambiguationData":[OSD([sQuery(id+"F0.wireOp",EDGE,"E0"),sQuery(id+"F0.wireOp",EDGE,"E1"),sQuery(id+"F0.wireOp",EDGE,"E3"),sQuery(id+"F0.wireOp",EDGE,"E5"),sQuery(id+"F0.wireOp",EDGE,"E7"),sQuery(id+"F0.wireOp",EDGE,"E8.1.3"),sQuery(id+"F0.wireOp",EDGE,"E8.1.4"),sQuery(id+"F0.wireOp",EDGE,"E8.1.5"),sQuery(id+"F0.wireOp",EDGE,"E8.2.3"),sQuery(id+"F0.wireOp",EDGE,"E8.2.4"),sQuery(id+"F0.wireOp",EDGE,"E8.2.5"),sQuery(id+"F0.wireOp",EDGE,"E9.11.3.0"),sQuery(id+"F0.wireOp",EDGE,"E9.15.3.0"),sQuery(id+"F0.wireOp",EDGE,"E9.19.3.0"),sQuery(id+"F0.wireOp",EDGE,"E9.11.4.0"),sQuery(id+"F0.wireOp",EDGE,"E9.15.4.0"),sQuery(id+"F0.wireOp",EDGE,"E9.19.4.0"),sQuery(id+"F0.wireOp",EDGE,"E9.11.5.0"),sQuery(id+"F0.wireOp",EDGE,"E9.15.5.0"),sQuery(id+"F0.wireOp",EDGE,"E9.19.5.0"),sQuery(id+"F0.wireOp",EDGE,"E9.11.6.0"),sQuery(id+"F0.wireOp",EDGE,"E9.15.6.0"),sQuery(id+"F0.wireOp",EDGE,"E9.19.6.0"),sQuery(id+"F0.wireOp",EDGE,"E9.11.7.0"),sQuery(id+"F0.wireOp",EDGE,"E9.15.7.0"),sQuery(id+"F0.wireOp",EDGE,"E9.19.7.0"),sQuery(id+"F0.wireOp",EDGE,"E9.11.8.0"),sQuery(id+"F0.wireOp",EDGE,"E9.15.8.0"),sQuery(id+"F0.wireOp",EDGE,"E9.19.8.0"),sQuery(id+"F0.wireOp",EDGE,"E9.11.9.0"),sQuery(id+"F0.wireOp",EDGE,"E9.15.9.0"),sQuery(id+"F0.wireOp",EDGE,"E9.19.9.0"),sQuery(id+"F0.wireOp",EDGE,"E9.11.10.0"),sQuery(id+"F0.wireOp",EDGE,"E9.15.10.0"),sQuery(id+"F0.wireOp",EDGE,"E9.19.10.0"),sQuery(id+"F0.wireOp",EDGE,"E9.11.11.0"),sQuery(id+"F0.wireOp",EDGE,"E9.15.11.0"),sQuery(id+"F0.wireOp",EDGE,"E9.19.11.0"),sQuery(id+"F0.wireOp",EDGE,"E9.11.12.0"),sQuery(id+"F0.wireOp",EDGE,"E9.15.12.0"),sQuery(id+"F0.wireOp",EDGE,"E9.19.12.0"),sQuery(id+"F0.wireOp",EDGE,"E9.11.13.0"),sQuery(id+"F0.wireOp",EDGE,"E9.15.13.0"),sQuery(id+"F0.wireOp",EDGE,"E9.19.13.0"),sQuery(id+"F0.wireOp",EDGE,"E9.11.14.0"),sQuery(id+"F0.wireOp",EDGE,"E9.15.14.0"),sQuery(id+"F0.wireOp",EDGE,"E9.19.14.0"),sQuery(id+"F0.wireOp",EDGE,"E9.11.15.0"),sQuery(id+"F0.wireOp",EDGE,"E9.15.15.0"),sQuery(id+"F0.wireOp",EDGE,"E9.19.15.0"),sQuery(id+"F0.wireOp",EDGE,"E9.11.16.0"),sQuery(id+"F0.wireOp",EDGE,"E9.15.16.0"),sQuery(id+"F0.wireOp",EDGE,"E9.19.16.0"),sQuery(id+"F0.wireOp",EDGE,"E9.11.17.0"),sQuery(id+"F0.wireOp",EDGE,"E9.15.17.0"),sQuery(id+"F0.wireOp",EDGE,"E9.19.17.0"),sQuery(id+"F0.wireOp",EDGE,"E9.11.18.0"),sQuery(id+"F0.wireOp",EDGE,"E9.15.18.0"),sQuery(id+"F0.wireOp",EDGE,"E9.19.18.0"),sQuery(id+"F0.wireOp",EDGE,"E9.11.19.0"),sQuery(id+"F0.wireOp",EDGE,"E9.15.19.0"),sQuery(id+"F0.wireOp",EDGE,"E9.19.19.0"),sQuery(id+"F0.wireOp",EDGE,"E9.11.20.0"),sQuery(id+"F0.wireOp",EDGE,"E9.15.20.0"),sQuery(id+"F0.wireOp",EDGE,"E9.19.20.0")])]});
            transform(context, id + "F13", {"entities" : qUnion([Q0, Q1]), "transformType" : TransformType.TRANSLATION_3D, "dx" : 0 * mm, "dy" : 6.35 * mm, "dz" : 0 * mm, "makeCopy" : true});
        }
        {
            var Q0;
            Q0=makeQuery(id+"F13.opPattern","COPY",BODY,{"derivedFrom":makeQuery(id+"F2.opExtrude","SWEPT_BODY",BODY,{"disambiguationData":[OSD([sQuery(id+"F0.wireOp",EDGE,"E0"),sQuery(id+"F0.wireOp",EDGE,"E1"),sQuery(id+"F0.wireOp",EDGE,"E2"),sQuery(id+"F0.wireOp",EDGE,"E4"),sQuery(id+"F0.wireOp",EDGE,"E6"),sQuery(id+"F0.wireOp",EDGE,"E8.1.0"),sQuery(id+"F0.wireOp",EDGE,"E8.1.1"),sQuery(id+"F0.wireOp",EDGE,"E8.1.2"),sQuery(id+"F0.wireOp",EDGE,"E8.2.0"),sQuery(id+"F0.wireOp",EDGE,"E8.2.1"),sQuery(id+"F0.wireOp",EDGE,"E8.2.2"),sQuery(id+"F0.wireOp",EDGE,"E9.3.3.0"),sQuery(id+"F0.wireOp",EDGE,"E9.4.3.0"),sQuery(id+"F0.wireOp",EDGE,"E9.8.3.0"),sQuery(id+"F0.wireOp",EDGE,"E9.3.4.0"),sQuery(id+"F0.wireOp",EDGE,"E9.4.4.0"),sQuery(id+"F0.wireOp",EDGE,"E9.8.4.0"),sQuery(id+"F0.wireOp",EDGE,"E9.3.5.0"),sQuery(id+"F0.wireOp",EDGE,"E9.4.5.0"),sQuery(id+"F0.wireOp",EDGE,"E9.8.5.0"),sQuery(id+"F0.wireOp",EDGE,"E9.3.6.0"),sQuery(id+"F0.wireOp",EDGE,"E9.4.6.0"),sQuery(id+"F0.wireOp",EDGE,"E9.8.6.0"),sQuery(id+"F0.wireOp",EDGE,"E9.3.7.0"),sQuery(id+"F0.wireOp",EDGE,"E9.4.7.0"),sQuery(id+"F0.wireOp",EDGE,"E9.8.7.0"),sQuery(id+"F0.wireOp",EDGE,"E9.3.8.0"),sQuery(id+"F0.wireOp",EDGE,"E9.4.8.0"),sQuery(id+"F0.wireOp",EDGE,"E9.8.8.0"),sQuery(id+"F0.wireOp",EDGE,"E9.3.9.0"),sQuery(id+"F0.wireOp",EDGE,"E9.4.9.0"),sQuery(id+"F0.wireOp",EDGE,"E9.8.9.0"),sQuery(id+"F0.wireOp",EDGE,"E9.3.10.0"),sQuery(id+"F0.wireOp",EDGE,"E9.4.10.0"),sQuery(id+"F0.wireOp",EDGE,"E9.8.10.0"),sQuery(id+"F0.wireOp",EDGE,"E9.3.11.0"),sQuery(id+"F0.wireOp",EDGE,"E9.4.11.0"),sQuery(id+"F0.wireOp",EDGE,"E9.8.11.0"),sQuery(id+"F0.wireOp",EDGE,"E9.3.12.0"),sQuery(id+"F0.wireOp",EDGE,"E9.4.12.0"),sQuery(id+"F0.wireOp",EDGE,"E9.8.12.0"),sQuery(id+"F0.wireOp",EDGE,"E9.3.13.0"),sQuery(id+"F0.wireOp",EDGE,"E9.4.13.0"),sQuery(id+"F0.wireOp",EDGE,"E9.8.13.0"),sQuery(id+"F0.wireOp",EDGE,"E9.3.14.0"),sQuery(id+"F0.wireOp",EDGE,"E9.4.14.0"),sQuery(id+"F0.wireOp",EDGE,"E9.8.14.0"),sQuery(id+"F0.wireOp",EDGE,"E9.3.15.0"),sQuery(id+"F0.wireOp",EDGE,"E9.4.15.0"),sQuery(id+"F0.wireOp",EDGE,"E9.8.15.0"),sQuery(id+"F0.wireOp",EDGE,"E9.3.16.0"),sQuery(id+"F0.wireOp",EDGE,"E9.4.16.0"),sQuery(id+"F0.wireOp",EDGE,"E9.8.16.0"),sQuery(id+"F0.wireOp",EDGE,"E9.3.17.0"),sQuery(id+"F0.wireOp",EDGE,"E9.4.17.0"),sQuery(id+"F0.wireOp",EDGE,"E9.8.17.0"),sQuery(id+"F0.wireOp",EDGE,"E9.3.18.0"),sQuery(id+"F0.wireOp",EDGE,"E9.4.18.0"),sQuery(id+"F0.wireOp",EDGE,"E9.8.18.0"),sQuery(id+"F0.wireOp",EDGE,"E9.3.19.0"),sQuery(id+"F0.wireOp",EDGE,"E9.4.19.0"),sQuery(id+"F0.wireOp",EDGE,"E9.8.19.0"),sQuery(id+"F0.wireOp",EDGE,"E9.3.20.0"),sQuery(id+"F0.wireOp",EDGE,"E9.4.20.0"),sQuery(id+"F0.wireOp",EDGE,"E9.8.20.0"),sQuery(id+"F0.wireOp",EDGE,"E10"),sQuery(id+"F0.wireOp",EDGE,"E11.1.0"),sQuery(id+"F0.wireOp",EDGE,"E11.2.0"),sQuery(id+"F0.wireOp",EDGE,"E11.3.0"),sQuery(id+"F0.wireOp",EDGE,"E11.4.0"),sQuery(id+"F0.wireOp",EDGE,"E11.5.0"),sQuery(id+"F0.wireOp",EDGE,"E11.6.0"),sQuery(id+"F0.wireOp",EDGE,"E11.7.0"),sQuery(id+"F0.wireOp",EDGE,"E11.8.0"),sQuery(id+"F0.wireOp",EDGE,"E11.9.0"),sQuery(id+"F0.wireOp",EDGE,"E11.10.0"),sQuery(id+"F0.wireOp",EDGE,"E11.11.0"),sQuery(id+"F0.wireOp",EDGE,"E11.12.0"),sQuery(id+"F0.wireOp",EDGE,"E11.13.0"),sQuery(id+"F0.wireOp",EDGE,"E11.14.0"),sQuery(id+"F0.wireOp",EDGE,"E11.15.0"),sQuery(id+"F0.wireOp",EDGE,"E11.16.0"),sQuery(id+"F0.wireOp",EDGE,"E11.17.0"),sQuery(id+"F0.wireOp",EDGE,"E11.18.0"),sQuery(id+"F0.wireOp",EDGE,"E11.19.0"),sQuery(id+"F0.wireOp",EDGE,"E11.20.0")])]}),"instanceName":"1"});
            var Q1;
            Q1=makeQuery(id+"F13.opPattern","COPY",EDGE,{"derivedFrom":makeQuery(id+"F2.opExtrude","CAP_EDGE",EDGE,{"disambiguationData":[OSD([sQuery(id+"F0.wireOp",EDGE,"E1")])],"isStart":false}),"instanceName":"1"});
            transform(context, id + "F14", {"entities" : qUnion([Q0]), "transformType" : TransformType.ROTATION, "transformAxis" : qUnion([Q1]), "angle" : 4.3 * degree, "makeCopy" : false});
        }
        {
            var Q0;
            Q0=makeQuery(id+"F13.opPattern","COPY",BODY,{"derivedFrom":makeQuery(id+"F1.opExtrude","SWEPT_BODY",BODY,{"disambiguationData":[OSD([sQuery(id+"F0.wireOp",EDGE,"E0"),sQuery(id+"F0.wireOp",EDGE,"E1"),sQuery(id+"F0.wireOp",EDGE,"E3"),sQuery(id+"F0.wireOp",EDGE,"E5"),sQuery(id+"F0.wireOp",EDGE,"E7"),sQuery(id+"F0.wireOp",EDGE,"E8.1.3"),sQuery(id+"F0.wireOp",EDGE,"E8.1.4"),sQuery(id+"F0.wireOp",EDGE,"E8.1.5"),sQuery(id+"F0.wireOp",EDGE,"E8.2.3"),sQuery(id+"F0.wireOp",EDGE,"E8.2.4"),sQuery(id+"F0.wireOp",EDGE,"E8.2.5"),sQuery(id+"F0.wireOp",EDGE,"E9.11.3.0"),sQuery(id+"F0.wireOp",EDGE,"E9.15.3.0"),sQuery(id+"F0.wireOp",EDGE,"E9.19.3.0"),sQuery(id+"F0.wireOp",EDGE,"E9.11.4.0"),sQuery(id+"F0.wireOp",EDGE,"E9.15.4.0"),sQuery(id+"F0.wireOp",EDGE,"E9.19.4.0"),sQuery(id+"F0.wireOp",EDGE,"E9.11.5.0"),sQuery(id+"F0.wireOp",EDGE,"E9.15.5.0"),sQuery(id+"F0.wireOp",EDGE,"E9.19.5.0"),sQuery(id+"F0.wireOp",EDGE,"E9.11.6.0"),sQuery(id+"F0.wireOp",EDGE,"E9.15.6.0"),sQuery(id+"F0.wireOp",EDGE,"E9.19.6.0"),sQuery(id+"F0.wireOp",EDGE,"E9.11.7.0"),sQuery(id+"F0.wireOp",EDGE,"E9.15.7.0"),sQuery(id+"F0.wireOp",EDGE,"E9.19.7.0"),sQuery(id+"F0.wireOp",EDGE,"E9.11.8.0"),sQuery(id+"F0.wireOp",EDGE,"E9.15.8.0"),sQuery(id+"F0.wireOp",EDGE,"E9.19.8.0"),sQuery(id+"F0.wireOp",EDGE,"E9.11.9.0"),sQuery(id+"F0.wireOp",EDGE,"E9.15.9.0"),sQuery(id+"F0.wireOp",EDGE,"E9.19.9.0"),sQuery(id+"F0.wireOp",EDGE,"E9.11.10.0"),sQuery(id+"F0.wireOp",EDGE,"E9.15.10.0"),sQuery(id+"F0.wireOp",EDGE,"E9.19.10.0"),sQuery(id+"F0.wireOp",EDGE,"E9.11.11.0"),sQuery(id+"F0.wireOp",EDGE,"E9.15.11.0"),sQuery(id+"F0.wireOp",EDGE,"E9.19.11.0"),sQuery(id+"F0.wireOp",EDGE,"E9.11.12.0"),sQuery(id+"F0.wireOp",EDGE,"E9.15.12.0"),sQuery(id+"F0.wireOp",EDGE,"E9.19.12.0"),sQuery(id+"F0.wireOp",EDGE,"E9.11.13.0"),sQuery(id+"F0.wireOp",EDGE,"E9.15.13.0"),sQuery(id+"F0.wireOp",EDGE,"E9.19.13.0"),sQuery(id+"F0.wireOp",EDGE,"E9.11.14.0"),sQuery(id+"F0.wireOp",EDGE,"E9.15.14.0"),sQuery(id+"F0.wireOp",EDGE,"E9.19.14.0"),sQuery(id+"F0.wireOp",EDGE,"E9.11.15.0"),sQuery(id+"F0.wireOp",EDGE,"E9.15.15.0"),sQuery(id+"F0.wireOp",EDGE,"E9.19.15.0"),sQuery(id+"F0.wireOp",EDGE,"E9.11.16.0"),sQuery(id+"F0.wireOp",EDGE,"E9.15.16.0"),sQuery(id+"F0.wireOp",EDGE,"E9.19.16.0"),sQuery(id+"F0.wireOp",EDGE,"E9.11.17.0"),sQuery(id+"F0.wireOp",EDGE,"E9.15.17.0"),sQuery(id+"F0.wireOp",EDGE,"E9.19.17.0"),sQuery(id+"F0.wireOp",EDGE,"E9.11.18.0"),sQuery(id+"F0.wireOp",EDGE,"E9.15.18.0"),sQuery(id+"F0.wireOp",EDGE,"E9.19.18.0"),sQuery(id+"F0.wireOp",EDGE,"E9.11.19.0"),sQuery(id+"F0.wireOp",EDGE,"E9.15.19.0"),sQuery(id+"F0.wireOp",EDGE,"E9.19.19.0"),sQuery(id+"F0.wireOp",EDGE,"E9.11.20.0"),sQuery(id+"F0.wireOp",EDGE,"E9.15.20.0"),sQuery(id+"F0.wireOp",EDGE,"E9.19.20.0")])]}),"instanceName":"1"});
            var Q1;
            Q1=makeQuery(id+"F13.opPattern","COPY",EDGE,{"derivedFrom":makeQuery(id+"F1.opExtrude","CAP_EDGE",EDGE,{"disambiguationData":[OSD([sQuery(id+"F0.wireOp",EDGE,"E1")])],"isStart":false}),"instanceName":"1"});
            transform(context, id + "F15", {"entities" : qUnion([Q0]), "transformType" : TransformType.ROTATION, "transformAxis" : qUnion([Q1]), "angle" : 4.3 * degree, "oppositeDirection" : true, "makeCopy" : false});
        }
        {
            var Q0;
            Q0=makeQuery(id+"F13.opPattern","COPY",BODY,{"derivedFrom":makeQuery(id+"F2.opExtrude","SWEPT_BODY",BODY,{"disambiguationData":[OSD([sQuery(id+"F0.wireOp",EDGE,"E0"),sQuery(id+"F0.wireOp",EDGE,"E1"),sQuery(id+"F0.wireOp",EDGE,"E2"),sQuery(id+"F0.wireOp",EDGE,"E4"),sQuery(id+"F0.wireOp",EDGE,"E6"),sQuery(id+"F0.wireOp",EDGE,"E8.1.0"),sQuery(id+"F0.wireOp",EDGE,"E8.1.1"),sQuery(id+"F0.wireOp",EDGE,"E8.1.2"),sQuery(id+"F0.wireOp",EDGE,"E8.2.0"),sQuery(id+"F0.wireOp",EDGE,"E8.2.1"),sQuery(id+"F0.wireOp",EDGE,"E8.2.2"),sQuery(id+"F0.wireOp",EDGE,"E9.3.3.0"),sQuery(id+"F0.wireOp",EDGE,"E9.4.3.0"),sQuery(id+"F0.wireOp",EDGE,"E9.8.3.0"),sQuery(id+"F0.wireOp",EDGE,"E9.3.4.0"),sQuery(id+"F0.wireOp",EDGE,"E9.4.4.0"),sQuery(id+"F0.wireOp",EDGE,"E9.8.4.0"),sQuery(id+"F0.wireOp",EDGE,"E9.3.5.0"),sQuery(id+"F0.wireOp",EDGE,"E9.4.5.0"),sQuery(id+"F0.wireOp",EDGE,"E9.8.5.0"),sQuery(id+"F0.wireOp",EDGE,"E9.3.6.0"),sQuery(id+"F0.wireOp",EDGE,"E9.4.6.0"),sQuery(id+"F0.wireOp",EDGE,"E9.8.6.0"),sQuery(id+"F0.wireOp",EDGE,"E9.3.7.0"),sQuery(id+"F0.wireOp",EDGE,"E9.4.7.0"),sQuery(id+"F0.wireOp",EDGE,"E9.8.7.0"),sQuery(id+"F0.wireOp",EDGE,"E9.3.8.0"),sQuery(id+"F0.wireOp",EDGE,"E9.4.8.0"),sQuery(id+"F0.wireOp",EDGE,"E9.8.8.0"),sQuery(id+"F0.wireOp",EDGE,"E9.3.9.0"),sQuery(id+"F0.wireOp",EDGE,"E9.4.9.0"),sQuery(id+"F0.wireOp",EDGE,"E9.8.9.0"),sQuery(id+"F0.wireOp",EDGE,"E9.3.10.0"),sQuery(id+"F0.wireOp",EDGE,"E9.4.10.0"),sQuery(id+"F0.wireOp",EDGE,"E9.8.10.0"),sQuery(id+"F0.wireOp",EDGE,"E9.3.11.0"),sQuery(id+"F0.wireOp",EDGE,"E9.4.11.0"),sQuery(id+"F0.wireOp",EDGE,"E9.8.11.0"),sQuery(id+"F0.wireOp",EDGE,"E9.3.12.0"),sQuery(id+"F0.wireOp",EDGE,"E9.4.12.0"),sQuery(id+"F0.wireOp",EDGE,"E9.8.12.0"),sQuery(id+"F0.wireOp",EDGE,"E9.3.13.0"),sQuery(id+"F0.wireOp",EDGE,"E9.4.13.0"),sQuery(id+"F0.wireOp",EDGE,"E9.8.13.0"),sQuery(id+"F0.wireOp",EDGE,"E9.3.14.0"),sQuery(id+"F0.wireOp",EDGE,"E9.4.14.0"),sQuery(id+"F0.wireOp",EDGE,"E9.8.14.0"),sQuery(id+"F0.wireOp",EDGE,"E9.3.15.0"),sQuery(id+"F0.wireOp",EDGE,"E9.4.15.0"),sQuery(id+"F0.wireOp",EDGE,"E9.8.15.0"),sQuery(id+"F0.wireOp",EDGE,"E9.3.16.0"),sQuery(id+"F0.wireOp",EDGE,"E9.4.16.0"),sQuery(id+"F0.wireOp",EDGE,"E9.8.16.0"),sQuery(id+"F0.wireOp",EDGE,"E9.3.17.0"),sQuery(id+"F0.wireOp",EDGE,"E9.4.17.0"),sQuery(id+"F0.wireOp",EDGE,"E9.8.17.0"),sQuery(id+"F0.wireOp",EDGE,"E9.3.18.0"),sQuery(id+"F0.wireOp",EDGE,"E9.4.18.0"),sQuery(id+"F0.wireOp",EDGE,"E9.8.18.0"),sQuery(id+"F0.wireOp",EDGE,"E9.3.19.0"),sQuery(id+"F0.wireOp",EDGE,"E9.4.19.0"),sQuery(id+"F0.wireOp",EDGE,"E9.8.19.0"),sQuery(id+"F0.wireOp",EDGE,"E9.3.20.0"),sQuery(id+"F0.wireOp",EDGE,"E9.4.20.0"),sQuery(id+"F0.wireOp",EDGE,"E9.8.20.0"),sQuery(id+"F0.wireOp",EDGE,"E10"),sQuery(id+"F0.wireOp",EDGE,"E11.1.0"),sQuery(id+"F0.wireOp",EDGE,"E11.2.0"),sQuery(id+"F0.wireOp",EDGE,"E11.3.0"),sQuery(id+"F0.wireOp",EDGE,"E11.4.0"),sQuery(id+"F0.wireOp",EDGE,"E11.5.0"),sQuery(id+"F0.wireOp",EDGE,"E11.6.0"),sQuery(id+"F0.wireOp",EDGE,"E11.7.0"),sQuery(id+"F0.wireOp",EDGE,"E11.8.0"),sQuery(id+"F0.wireOp",EDGE,"E11.9.0"),sQuery(id+"F0.wireOp",EDGE,"E11.10.0"),sQuery(id+"F0.wireOp",EDGE,"E11.11.0"),sQuery(id+"F0.wireOp",EDGE,"E11.12.0"),sQuery(id+"F0.wireOp",EDGE,"E11.13.0"),sQuery(id+"F0.wireOp",EDGE,"E11.14.0"),sQuery(id+"F0.wireOp",EDGE,"E11.15.0"),sQuery(id+"F0.wireOp",EDGE,"E11.16.0"),sQuery(id+"F0.wireOp",EDGE,"E11.17.0"),sQuery(id+"F0.wireOp",EDGE,"E11.18.0"),sQuery(id+"F0.wireOp",EDGE,"E11.19.0"),sQuery(id+"F0.wireOp",EDGE,"E11.20.0")])]}),"instanceName":"1"});
            var Q1;
            Q1=makeQuery(id+"F13.opPattern","COPY",BODY,{"derivedFrom":makeQuery(id+"F1.opExtrude","SWEPT_BODY",BODY,{"disambiguationData":[OSD([sQuery(id+"F0.wireOp",EDGE,"E0"),sQuery(id+"F0.wireOp",EDGE,"E1"),sQuery(id+"F0.wireOp",EDGE,"E3"),sQuery(id+"F0.wireOp",EDGE,"E5"),sQuery(id+"F0.wireOp",EDGE,"E7"),sQuery(id+"F0.wireOp",EDGE,"E8.1.3"),sQuery(id+"F0.wireOp",EDGE,"E8.1.4"),sQuery(id+"F0.wireOp",EDGE,"E8.1.5"),sQuery(id+"F0.wireOp",EDGE,"E8.2.3"),sQuery(id+"F0.wireOp",EDGE,"E8.2.4"),sQuery(id+"F0.wireOp",EDGE,"E8.2.5"),sQuery(id+"F0.wireOp",EDGE,"E9.11.3.0"),sQuery(id+"F0.wireOp",EDGE,"E9.15.3.0"),sQuery(id+"F0.wireOp",EDGE,"E9.19.3.0"),sQuery(id+"F0.wireOp",EDGE,"E9.11.4.0"),sQuery(id+"F0.wireOp",EDGE,"E9.15.4.0"),sQuery(id+"F0.wireOp",EDGE,"E9.19.4.0"),sQuery(id+"F0.wireOp",EDGE,"E9.11.5.0"),sQuery(id+"F0.wireOp",EDGE,"E9.15.5.0"),sQuery(id+"F0.wireOp",EDGE,"E9.19.5.0"),sQuery(id+"F0.wireOp",EDGE,"E9.11.6.0"),sQuery(id+"F0.wireOp",EDGE,"E9.15.6.0"),sQuery(id+"F0.wireOp",EDGE,"E9.19.6.0"),sQuery(id+"F0.wireOp",EDGE,"E9.11.7.0"),sQuery(id+"F0.wireOp",EDGE,"E9.15.7.0"),sQuery(id+"F0.wireOp",EDGE,"E9.19.7.0"),sQuery(id+"F0.wireOp",EDGE,"E9.11.8.0"),sQuery(id+"F0.wireOp",EDGE,"E9.15.8.0"),sQuery(id+"F0.wireOp",EDGE,"E9.19.8.0"),sQuery(id+"F0.wireOp",EDGE,"E9.11.9.0"),sQuery(id+"F0.wireOp",EDGE,"E9.15.9.0"),sQuery(id+"F0.wireOp",EDGE,"E9.19.9.0"),sQuery(id+"F0.wireOp",EDGE,"E9.11.10.0"),sQuery(id+"F0.wireOp",EDGE,"E9.15.10.0"),sQuery(id+"F0.wireOp",EDGE,"E9.19.10.0"),sQuery(id+"F0.wireOp",EDGE,"E9.11.11.0"),sQuery(id+"F0.wireOp",EDGE,"E9.15.11.0"),sQuery(id+"F0.wireOp",EDGE,"E9.19.11.0"),sQuery(id+"F0.wireOp",EDGE,"E9.11.12.0"),sQuery(id+"F0.wireOp",EDGE,"E9.15.12.0"),sQuery(id+"F0.wireOp",EDGE,"E9.19.12.0"),sQuery(id+"F0.wireOp",EDGE,"E9.11.13.0"),sQuery(id+"F0.wireOp",EDGE,"E9.15.13.0"),sQuery(id+"F0.wireOp",EDGE,"E9.19.13.0"),sQuery(id+"F0.wireOp",EDGE,"E9.11.14.0"),sQuery(id+"F0.wireOp",EDGE,"E9.15.14.0"),sQuery(id+"F0.wireOp",EDGE,"E9.19.14.0"),sQuery(id+"F0.wireOp",EDGE,"E9.11.15.0"),sQuery(id+"F0.wireOp",EDGE,"E9.15.15.0"),sQuery(id+"F0.wireOp",EDGE,"E9.19.15.0"),sQuery(id+"F0.wireOp",EDGE,"E9.11.16.0"),sQuery(id+"F0.wireOp",EDGE,"E9.15.16.0"),sQuery(id+"F0.wireOp",EDGE,"E9.19.16.0"),sQuery(id+"F0.wireOp",EDGE,"E9.11.17.0"),sQuery(id+"F0.wireOp",EDGE,"E9.15.17.0"),sQuery(id+"F0.wireOp",EDGE,"E9.19.17.0"),sQuery(id+"F0.wireOp",EDGE,"E9.11.18.0"),sQuery(id+"F0.wireOp",EDGE,"E9.15.18.0"),sQuery(id+"F0.wireOp",EDGE,"E9.19.18.0"),sQuery(id+"F0.wireOp",EDGE,"E9.11.19.0"),sQuery(id+"F0.wireOp",EDGE,"E9.15.19.0"),sQuery(id+"F0.wireOp",EDGE,"E9.19.19.0"),sQuery(id+"F0.wireOp",EDGE,"E9.11.20.0"),sQuery(id+"F0.wireOp",EDGE,"E9.15.20.0"),sQuery(id+"F0.wireOp",EDGE,"E9.19.20.0")])]}),"instanceName":"1"});
            transform(context, id + "F16", {"entities" : qUnion([Q0, Q1]), "transformType" : TransformType.TRANSLATION_3D, "dx" : 0 * mm, "dy" : 6.35 * mm, "dz" : 0 * mm, "makeCopy" : true});
        }
        {
            var Q0;
            Q0=makeQuery(id+"F16.opPattern","COPY",BODY,{"derivedFrom":makeQuery(id+"F13.opPattern","COPY",BODY,{"derivedFrom":makeQuery(id+"F2.opExtrude","SWEPT_BODY",BODY,{"disambiguationData":[OSD([sQuery(id+"F0.wireOp",EDGE,"E0"),sQuery(id+"F0.wireOp",EDGE,"E1"),sQuery(id+"F0.wireOp",EDGE,"E2"),sQuery(id+"F0.wireOp",EDGE,"E4"),sQuery(id+"F0.wireOp",EDGE,"E6"),sQuery(id+"F0.wireOp",EDGE,"E8.1.0"),sQuery(id+"F0.wireOp",EDGE,"E8.1.1"),sQuery(id+"F0.wireOp",EDGE,"E8.1.2"),sQuery(id+"F0.wireOp",EDGE,"E8.2.0"),sQuery(id+"F0.wireOp",EDGE,"E8.2.1"),sQuery(id+"F0.wireOp",EDGE,"E8.2.2"),sQuery(id+"F0.wireOp",EDGE,"E9.3.3.0"),sQuery(id+"F0.wireOp",EDGE,"E9.4.3.0"),sQuery(id+"F0.wireOp",EDGE,"E9.8.3.0"),sQuery(id+"F0.wireOp",EDGE,"E9.3.4.0"),sQuery(id+"F0.wireOp",EDGE,"E9.4.4.0"),sQuery(id+"F0.wireOp",EDGE,"E9.8.4.0"),sQuery(id+"F0.wireOp",EDGE,"E9.3.5.0"),sQuery(id+"F0.wireOp",EDGE,"E9.4.5.0"),sQuery(id+"F0.wireOp",EDGE,"E9.8.5.0"),sQuery(id+"F0.wireOp",EDGE,"E9.3.6.0"),sQuery(id+"F0.wireOp",EDGE,"E9.4.6.0"),sQuery(id+"F0.wireOp",EDGE,"E9.8.6.0"),sQuery(id+"F0.wireOp",EDGE,"E9.3.7.0"),sQuery(id+"F0.wireOp",EDGE,"E9.4.7.0"),sQuery(id+"F0.wireOp",EDGE,"E9.8.7.0"),sQuery(id+"F0.wireOp",EDGE,"E9.3.8.0"),sQuery(id+"F0.wireOp",EDGE,"E9.4.8.0"),sQuery(id+"F0.wireOp",EDGE,"E9.8.8.0"),sQuery(id+"F0.wireOp",EDGE,"E9.3.9.0"),sQuery(id+"F0.wireOp",EDGE,"E9.4.9.0"),sQuery(id+"F0.wireOp",EDGE,"E9.8.9.0"),sQuery(id+"F0.wireOp",EDGE,"E9.3.10.0"),sQuery(id+"F0.wireOp",EDGE,"E9.4.10.0"),sQuery(id+"F0.wireOp",EDGE,"E9.8.10.0"),sQuery(id+"F0.wireOp",EDGE,"E9.3.11.0"),sQuery(id+"F0.wireOp",EDGE,"E9.4.11.0"),sQuery(id+"F0.wireOp",EDGE,"E9.8.11.0"),sQuery(id+"F0.wireOp",EDGE,"E9.3.12.0"),sQuery(id+"F0.wireOp",EDGE,"E9.4.12.0"),sQuery(id+"F0.wireOp",EDGE,"E9.8.12.0"),sQuery(id+"F0.wireOp",EDGE,"E9.3.13.0"),sQuery(id+"F0.wireOp",EDGE,"E9.4.13.0"),sQuery(id+"F0.wireOp",EDGE,"E9.8.13.0"),sQuery(id+"F0.wireOp",EDGE,"E9.3.14.0"),sQuery(id+"F0.wireOp",EDGE,"E9.4.14.0"),sQuery(id+"F0.wireOp",EDGE,"E9.8.14.0"),sQuery(id+"F0.wireOp",EDGE,"E9.3.15.0"),sQuery(id+"F0.wireOp",EDGE,"E9.4.15.0"),sQuery(id+"F0.wireOp",EDGE,"E9.8.15.0"),sQuery(id+"F0.wireOp",EDGE,"E9.3.16.0"),sQuery(id+"F0.wireOp",EDGE,"E9.4.16.0"),sQuery(id+"F0.wireOp",EDGE,"E9.8.16.0"),sQuery(id+"F0.wireOp",EDGE,"E9.3.17.0"),sQuery(id+"F0.wireOp",EDGE,"E9.4.17.0"),sQuery(id+"F0.wireOp",EDGE,"E9.8.17.0"),sQuery(id+"F0.wireOp",EDGE,"E9.3.18.0"),sQuery(id+"F0.wireOp",EDGE,"E9.4.18.0"),sQuery(id+"F0.wireOp",EDGE,"E9.8.18.0"),sQuery(id+"F0.wireOp",EDGE,"E9.3.19.0"),sQuery(id+"F0.wireOp",EDGE,"E9.4.19.0"),sQuery(id+"F0.wireOp",EDGE,"E9.8.19.0"),sQuery(id+"F0.wireOp",EDGE,"E9.3.20.0"),sQuery(id+"F0.wireOp",EDGE,"E9.4.20.0"),sQuery(id+"F0.wireOp",EDGE,"E9.8.20.0"),sQuery(id+"F0.wireOp",EDGE,"E10"),sQuery(id+"F0.wireOp",EDGE,"E11.1.0"),sQuery(id+"F0.wireOp",EDGE,"E11.2.0"),sQuery(id+"F0.wireOp",EDGE,"E11.3.0"),sQuery(id+"F0.wireOp",EDGE,"E11.4.0"),sQuery(id+"F0.wireOp",EDGE,"E11.5.0"),sQuery(id+"F0.wireOp",EDGE,"E11.6.0"),sQuery(id+"F0.wireOp",EDGE,"E11.7.0"),sQuery(id+"F0.wireOp",EDGE,"E11.8.0"),sQuery(id+"F0.wireOp",EDGE,"E11.9.0"),sQuery(id+"F0.wireOp",EDGE,"E11.10.0"),sQuery(id+"F0.wireOp",EDGE,"E11.11.0"),sQuery(id+"F0.wireOp",EDGE,"E11.12.0"),sQuery(id+"F0.wireOp",EDGE,"E11.13.0"),sQuery(id+"F0.wireOp",EDGE,"E11.14.0"),sQuery(id+"F0.wireOp",EDGE,"E11.15.0"),sQuery(id+"F0.wireOp",EDGE,"E11.16.0"),sQuery(id+"F0.wireOp",EDGE,"E11.17.0"),sQuery(id+"F0.wireOp",EDGE,"E11.18.0"),sQuery(id+"F0.wireOp",EDGE,"E11.19.0"),sQuery(id+"F0.wireOp",EDGE,"E11.20.0")])]}),"instanceName":"1"}),"instanceName":"1"});
            var Q1;
            Q1=makeQuery(id+"F16.opPattern","COPY",EDGE,{"derivedFrom":makeQuery(id+"F13.opPattern","COPY",EDGE,{"derivedFrom":makeQuery(id+"F2.opExtrude","CAP_EDGE",EDGE,{"disambiguationData":[OSD([sQuery(id+"F0.wireOp",EDGE,"E1")])],"isStart":false}),"instanceName":"1"}),"instanceName":"1"});
            transform(context, id + "F17", {"entities" : qUnion([Q0]), "transformType" : TransformType.ROTATION, "transformAxis" : qUnion([Q1]), "angle" : 4.3 * degree, "makeCopy" : false});
        }
        {
            var Q0;
            Q0=makeQuery(id+"F16.opPattern","COPY",BODY,{"derivedFrom":makeQuery(id+"F13.opPattern","COPY",BODY,{"derivedFrom":makeQuery(id+"F1.opExtrude","SWEPT_BODY",BODY,{"disambiguationData":[OSD([sQuery(id+"F0.wireOp",EDGE,"E0"),sQuery(id+"F0.wireOp",EDGE,"E1"),sQuery(id+"F0.wireOp",EDGE,"E3"),sQuery(id+"F0.wireOp",EDGE,"E5"),sQuery(id+"F0.wireOp",EDGE,"E7"),sQuery(id+"F0.wireOp",EDGE,"E8.1.3"),sQuery(id+"F0.wireOp",EDGE,"E8.1.4"),sQuery(id+"F0.wireOp",EDGE,"E8.1.5"),sQuery(id+"F0.wireOp",EDGE,"E8.2.3"),sQuery(id+"F0.wireOp",EDGE,"E8.2.4"),sQuery(id+"F0.wireOp",EDGE,"E8.2.5"),sQuery(id+"F0.wireOp",EDGE,"E9.11.3.0"),sQuery(id+"F0.wireOp",EDGE,"E9.15.3.0"),sQuery(id+"F0.wireOp",EDGE,"E9.19.3.0"),sQuery(id+"F0.wireOp",EDGE,"E9.11.4.0"),sQuery(id+"F0.wireOp",EDGE,"E9.15.4.0"),sQuery(id+"F0.wireOp",EDGE,"E9.19.4.0"),sQuery(id+"F0.wireOp",EDGE,"E9.11.5.0"),sQuery(id+"F0.wireOp",EDGE,"E9.15.5.0"),sQuery(id+"F0.wireOp",EDGE,"E9.19.5.0"),sQuery(id+"F0.wireOp",EDGE,"E9.11.6.0"),sQuery(id+"F0.wireOp",EDGE,"E9.15.6.0"),sQuery(id+"F0.wireOp",EDGE,"E9.19.6.0"),sQuery(id+"F0.wireOp",EDGE,"E9.11.7.0"),sQuery(id+"F0.wireOp",EDGE,"E9.15.7.0"),sQuery(id+"F0.wireOp",EDGE,"E9.19.7.0"),sQuery(id+"F0.wireOp",EDGE,"E9.11.8.0"),sQuery(id+"F0.wireOp",EDGE,"E9.15.8.0"),sQuery(id+"F0.wireOp",EDGE,"E9.19.8.0"),sQuery(id+"F0.wireOp",EDGE,"E9.11.9.0"),sQuery(id+"F0.wireOp",EDGE,"E9.15.9.0"),sQuery(id+"F0.wireOp",EDGE,"E9.19.9.0"),sQuery(id+"F0.wireOp",EDGE,"E9.11.10.0"),sQuery(id+"F0.wireOp",EDGE,"E9.15.10.0"),sQuery(id+"F0.wireOp",EDGE,"E9.19.10.0"),sQuery(id+"F0.wireOp",EDGE,"E9.11.11.0"),sQuery(id+"F0.wireOp",EDGE,"E9.15.11.0"),sQuery(id+"F0.wireOp",EDGE,"E9.19.11.0"),sQuery(id+"F0.wireOp",EDGE,"E9.11.12.0"),sQuery(id+"F0.wireOp",EDGE,"E9.15.12.0"),sQuery(id+"F0.wireOp",EDGE,"E9.19.12.0"),sQuery(id+"F0.wireOp",EDGE,"E9.11.13.0"),sQuery(id+"F0.wireOp",EDGE,"E9.15.13.0"),sQuery(id+"F0.wireOp",EDGE,"E9.19.13.0"),sQuery(id+"F0.wireOp",EDGE,"E9.11.14.0"),sQuery(id+"F0.wireOp",EDGE,"E9.15.14.0"),sQuery(id+"F0.wireOp",EDGE,"E9.19.14.0"),sQuery(id+"F0.wireOp",EDGE,"E9.11.15.0"),sQuery(id+"F0.wireOp",EDGE,"E9.15.15.0"),sQuery(id+"F0.wireOp",EDGE,"E9.19.15.0"),sQuery(id+"F0.wireOp",EDGE,"E9.11.16.0"),sQuery(id+"F0.wireOp",EDGE,"E9.15.16.0"),sQuery(id+"F0.wireOp",EDGE,"E9.19.16.0"),sQuery(id+"F0.wireOp",EDGE,"E9.11.17.0"),sQuery(id+"F0.wireOp",EDGE,"E9.15.17.0"),sQuery(id+"F0.wireOp",EDGE,"E9.19.17.0"),sQuery(id+"F0.wireOp",EDGE,"E9.11.18.0"),sQuery(id+"F0.wireOp",EDGE,"E9.15.18.0"),sQuery(id+"F0.wireOp",EDGE,"E9.19.18.0"),sQuery(id+"F0.wireOp",EDGE,"E9.11.19.0"),sQuery(id+"F0.wireOp",EDGE,"E9.15.19.0"),sQuery(id+"F0.wireOp",EDGE,"E9.19.19.0"),sQuery(id+"F0.wireOp",EDGE,"E9.11.20.0"),sQuery(id+"F0.wireOp",EDGE,"E9.15.20.0"),sQuery(id+"F0.wireOp",EDGE,"E9.19.20.0")])]}),"instanceName":"1"}),"instanceName":"1"});
            var Q1;
            Q1=makeQuery(id+"F16.opPattern","COPY",EDGE,{"derivedFrom":makeQuery(id+"F13.opPattern","COPY",EDGE,{"derivedFrom":makeQuery(id+"F1.opExtrude","CAP_EDGE",EDGE,{"disambiguationData":[OSD([sQuery(id+"F0.wireOp",EDGE,"E1")])],"isStart":false}),"instanceName":"1"}),"instanceName":"1"});
            transform(context, id + "F18", {"entities" : qUnion([Q0]), "transformType" : TransformType.ROTATION, "transformAxis" : qUnion([Q1]), "angle" : 4.3 * degree, "oppositeDirection" : true, "makeCopy" : false});
        }
        {
            var Q0;
            Q0=makeQuery(id+"F16.opPattern","COPY",BODY,{"derivedFrom":makeQuery(id+"F13.opPattern","COPY",BODY,{"derivedFrom":makeQuery(id+"F2.opExtrude","SWEPT_BODY",BODY,{"disambiguationData":[OSD([sQuery(id+"F0.wireOp",EDGE,"E0"),sQuery(id+"F0.wireOp",EDGE,"E1"),sQuery(id+"F0.wireOp",EDGE,"E2"),sQuery(id+"F0.wireOp",EDGE,"E4"),sQuery(id+"F0.wireOp",EDGE,"E6"),sQuery(id+"F0.wireOp",EDGE,"E8.1.0"),sQuery(id+"F0.wireOp",EDGE,"E8.1.1"),sQuery(id+"F0.wireOp",EDGE,"E8.1.2"),sQuery(id+"F0.wireOp",EDGE,"E8.2.0"),sQuery(id+"F0.wireOp",EDGE,"E8.2.1"),sQuery(id+"F0.wireOp",EDGE,"E8.2.2"),sQuery(id+"F0.wireOp",EDGE,"E9.3.3.0"),sQuery(id+"F0.wireOp",EDGE,"E9.4.3.0"),sQuery(id+"F0.wireOp",EDGE,"E9.8.3.0"),sQuery(id+"F0.wireOp",EDGE,"E9.3.4.0"),sQuery(id+"F0.wireOp",EDGE,"E9.4.4.0"),sQuery(id+"F0.wireOp",EDGE,"E9.8.4.0"),sQuery(id+"F0.wireOp",EDGE,"E9.3.5.0"),sQuery(id+"F0.wireOp",EDGE,"E9.4.5.0"),sQuery(id+"F0.wireOp",EDGE,"E9.8.5.0"),sQuery(id+"F0.wireOp",EDGE,"E9.3.6.0"),sQuery(id+"F0.wireOp",EDGE,"E9.4.6.0"),sQuery(id+"F0.wireOp",EDGE,"E9.8.6.0"),sQuery(id+"F0.wireOp",EDGE,"E9.3.7.0"),sQuery(id+"F0.wireOp",EDGE,"E9.4.7.0"),sQuery(id+"F0.wireOp",EDGE,"E9.8.7.0"),sQuery(id+"F0.wireOp",EDGE,"E9.3.8.0"),sQuery(id+"F0.wireOp",EDGE,"E9.4.8.0"),sQuery(id+"F0.wireOp",EDGE,"E9.8.8.0"),sQuery(id+"F0.wireOp",EDGE,"E9.3.9.0"),sQuery(id+"F0.wireOp",EDGE,"E9.4.9.0"),sQuery(id+"F0.wireOp",EDGE,"E9.8.9.0"),sQuery(id+"F0.wireOp",EDGE,"E9.3.10.0"),sQuery(id+"F0.wireOp",EDGE,"E9.4.10.0"),sQuery(id+"F0.wireOp",EDGE,"E9.8.10.0"),sQuery(id+"F0.wireOp",EDGE,"E9.3.11.0"),sQuery(id+"F0.wireOp",EDGE,"E9.4.11.0"),sQuery(id+"F0.wireOp",EDGE,"E9.8.11.0"),sQuery(id+"F0.wireOp",EDGE,"E9.3.12.0"),sQuery(id+"F0.wireOp",EDGE,"E9.4.12.0"),sQuery(id+"F0.wireOp",EDGE,"E9.8.12.0"),sQuery(id+"F0.wireOp",EDGE,"E9.3.13.0"),sQuery(id+"F0.wireOp",EDGE,"E9.4.13.0"),sQuery(id+"F0.wireOp",EDGE,"E9.8.13.0"),sQuery(id+"F0.wireOp",EDGE,"E9.3.14.0"),sQuery(id+"F0.wireOp",EDGE,"E9.4.14.0"),sQuery(id+"F0.wireOp",EDGE,"E9.8.14.0"),sQuery(id+"F0.wireOp",EDGE,"E9.3.15.0"),sQuery(id+"F0.wireOp",EDGE,"E9.4.15.0"),sQuery(id+"F0.wireOp",EDGE,"E9.8.15.0"),sQuery(id+"F0.wireOp",EDGE,"E9.3.16.0"),sQuery(id+"F0.wireOp",EDGE,"E9.4.16.0"),sQuery(id+"F0.wireOp",EDGE,"E9.8.16.0"),sQuery(id+"F0.wireOp",EDGE,"E9.3.17.0"),sQuery(id+"F0.wireOp",EDGE,"E9.4.17.0"),sQuery(id+"F0.wireOp",EDGE,"E9.8.17.0"),sQuery(id+"F0.wireOp",EDGE,"E9.3.18.0"),sQuery(id+"F0.wireOp",EDGE,"E9.4.18.0"),sQuery(id+"F0.wireOp",EDGE,"E9.8.18.0"),sQuery(id+"F0.wireOp",EDGE,"E9.3.19.0"),sQuery(id+"F0.wireOp",EDGE,"E9.4.19.0"),sQuery(id+"F0.wireOp",EDGE,"E9.8.19.0"),sQuery(id+"F0.wireOp",EDGE,"E9.3.20.0"),sQuery(id+"F0.wireOp",EDGE,"E9.4.20.0"),sQuery(id+"F0.wireOp",EDGE,"E9.8.20.0"),sQuery(id+"F0.wireOp",EDGE,"E10"),sQuery(id+"F0.wireOp",EDGE,"E11.1.0"),sQuery(id+"F0.wireOp",EDGE,"E11.2.0"),sQuery(id+"F0.wireOp",EDGE,"E11.3.0"),sQuery(id+"F0.wireOp",EDGE,"E11.4.0"),sQuery(id+"F0.wireOp",EDGE,"E11.5.0"),sQuery(id+"F0.wireOp",EDGE,"E11.6.0"),sQuery(id+"F0.wireOp",EDGE,"E11.7.0"),sQuery(id+"F0.wireOp",EDGE,"E11.8.0"),sQuery(id+"F0.wireOp",EDGE,"E11.9.0"),sQuery(id+"F0.wireOp",EDGE,"E11.10.0"),sQuery(id+"F0.wireOp",EDGE,"E11.11.0"),sQuery(id+"F0.wireOp",EDGE,"E11.12.0"),sQuery(id+"F0.wireOp",EDGE,"E11.13.0"),sQuery(id+"F0.wireOp",EDGE,"E11.14.0"),sQuery(id+"F0.wireOp",EDGE,"E11.15.0"),sQuery(id+"F0.wireOp",EDGE,"E11.16.0"),sQuery(id+"F0.wireOp",EDGE,"E11.17.0"),sQuery(id+"F0.wireOp",EDGE,"E11.18.0"),sQuery(id+"F0.wireOp",EDGE,"E11.19.0"),sQuery(id+"F0.wireOp",EDGE,"E11.20.0")])]}),"instanceName":"1"}),"instanceName":"1"});
            var Q1;
            Q1=makeQuery(id+"F16.opPattern","COPY",BODY,{"derivedFrom":makeQuery(id+"F13.opPattern","COPY",BODY,{"derivedFrom":makeQuery(id+"F1.opExtrude","SWEPT_BODY",BODY,{"disambiguationData":[OSD([sQuery(id+"F0.wireOp",EDGE,"E0"),sQuery(id+"F0.wireOp",EDGE,"E1"),sQuery(id+"F0.wireOp",EDGE,"E3"),sQuery(id+"F0.wireOp",EDGE,"E5"),sQuery(id+"F0.wireOp",EDGE,"E7"),sQuery(id+"F0.wireOp",EDGE,"E8.1.3"),sQuery(id+"F0.wireOp",EDGE,"E8.1.4"),sQuery(id+"F0.wireOp",EDGE,"E8.1.5"),sQuery(id+"F0.wireOp",EDGE,"E8.2.3"),sQuery(id+"F0.wireOp",EDGE,"E8.2.4"),sQuery(id+"F0.wireOp",EDGE,"E8.2.5"),sQuery(id+"F0.wireOp",EDGE,"E9.11.3.0"),sQuery(id+"F0.wireOp",EDGE,"E9.15.3.0"),sQuery(id+"F0.wireOp",EDGE,"E9.19.3.0"),sQuery(id+"F0.wireOp",EDGE,"E9.11.4.0"),sQuery(id+"F0.wireOp",EDGE,"E9.15.4.0"),sQuery(id+"F0.wireOp",EDGE,"E9.19.4.0"),sQuery(id+"F0.wireOp",EDGE,"E9.11.5.0"),sQuery(id+"F0.wireOp",EDGE,"E9.15.5.0"),sQuery(id+"F0.wireOp",EDGE,"E9.19.5.0"),sQuery(id+"F0.wireOp",EDGE,"E9.11.6.0"),sQuery(id+"F0.wireOp",EDGE,"E9.15.6.0"),sQuery(id+"F0.wireOp",EDGE,"E9.19.6.0"),sQuery(id+"F0.wireOp",EDGE,"E9.11.7.0"),sQuery(id+"F0.wireOp",EDGE,"E9.15.7.0"),sQuery(id+"F0.wireOp",EDGE,"E9.19.7.0"),sQuery(id+"F0.wireOp",EDGE,"E9.11.8.0"),sQuery(id+"F0.wireOp",EDGE,"E9.15.8.0"),sQuery(id+"F0.wireOp",EDGE,"E9.19.8.0"),sQuery(id+"F0.wireOp",EDGE,"E9.11.9.0"),sQuery(id+"F0.wireOp",EDGE,"E9.15.9.0"),sQuery(id+"F0.wireOp",EDGE,"E9.19.9.0"),sQuery(id+"F0.wireOp",EDGE,"E9.11.10.0"),sQuery(id+"F0.wireOp",EDGE,"E9.15.10.0"),sQuery(id+"F0.wireOp",EDGE,"E9.19.10.0"),sQuery(id+"F0.wireOp",EDGE,"E9.11.11.0"),sQuery(id+"F0.wireOp",EDGE,"E9.15.11.0"),sQuery(id+"F0.wireOp",EDGE,"E9.19.11.0"),sQuery(id+"F0.wireOp",EDGE,"E9.11.12.0"),sQuery(id+"F0.wireOp",EDGE,"E9.15.12.0"),sQuery(id+"F0.wireOp",EDGE,"E9.19.12.0"),sQuery(id+"F0.wireOp",EDGE,"E9.11.13.0"),sQuery(id+"F0.wireOp",EDGE,"E9.15.13.0"),sQuery(id+"F0.wireOp",EDGE,"E9.19.13.0"),sQuery(id+"F0.wireOp",EDGE,"E9.11.14.0"),sQuery(id+"F0.wireOp",EDGE,"E9.15.14.0"),sQuery(id+"F0.wireOp",EDGE,"E9.19.14.0"),sQuery(id+"F0.wireOp",EDGE,"E9.11.15.0"),sQuery(id+"F0.wireOp",EDGE,"E9.15.15.0"),sQuery(id+"F0.wireOp",EDGE,"E9.19.15.0"),sQuery(id+"F0.wireOp",EDGE,"E9.11.16.0"),sQuery(id+"F0.wireOp",EDGE,"E9.15.16.0"),sQuery(id+"F0.wireOp",EDGE,"E9.19.16.0"),sQuery(id+"F0.wireOp",EDGE,"E9.11.17.0"),sQuery(id+"F0.wireOp",EDGE,"E9.15.17.0"),sQuery(id+"F0.wireOp",EDGE,"E9.19.17.0"),sQuery(id+"F0.wireOp",EDGE,"E9.11.18.0"),sQuery(id+"F0.wireOp",EDGE,"E9.15.18.0"),sQuery(id+"F0.wireOp",EDGE,"E9.19.18.0"),sQuery(id+"F0.wireOp",EDGE,"E9.11.19.0"),sQuery(id+"F0.wireOp",EDGE,"E9.15.19.0"),sQuery(id+"F0.wireOp",EDGE,"E9.19.19.0"),sQuery(id+"F0.wireOp",EDGE,"E9.11.20.0"),sQuery(id+"F0.wireOp",EDGE,"E9.15.20.0"),sQuery(id+"F0.wireOp",EDGE,"E9.19.20.0")])]}),"instanceName":"1"}),"instanceName":"1"});
            transform(context, id + "F19", {"entities" : qUnion([Q0, Q1]), "transformType" : TransformType.TRANSLATION_3D, "dx" : 0 * mm, "dy" : 6.35 * mm, "dz" : 0 * mm, "makeCopy" : true});
        }
        {
            var Q0;
            Q0=makeQuery(id+"F19.opPattern","COPY",BODY,{"derivedFrom":makeQuery(id+"F16.opPattern","COPY",BODY,{"derivedFrom":makeQuery(id+"F13.opPattern","COPY",BODY,{"derivedFrom":makeQuery(id+"F2.opExtrude","SWEPT_BODY",BODY,{"disambiguationData":[OSD([sQuery(id+"F0.wireOp",EDGE,"E0"),sQuery(id+"F0.wireOp",EDGE,"E1"),sQuery(id+"F0.wireOp",EDGE,"E2"),sQuery(id+"F0.wireOp",EDGE,"E4"),sQuery(id+"F0.wireOp",EDGE,"E6"),sQuery(id+"F0.wireOp",EDGE,"E8.1.0"),sQuery(id+"F0.wireOp",EDGE,"E8.1.1"),sQuery(id+"F0.wireOp",EDGE,"E8.1.2"),sQuery(id+"F0.wireOp",EDGE,"E8.2.0"),sQuery(id+"F0.wireOp",EDGE,"E8.2.1"),sQuery(id+"F0.wireOp",EDGE,"E8.2.2"),sQuery(id+"F0.wireOp",EDGE,"E9.3.3.0"),sQuery(id+"F0.wireOp",EDGE,"E9.4.3.0"),sQuery(id+"F0.wireOp",EDGE,"E9.8.3.0"),sQuery(id+"F0.wireOp",EDGE,"E9.3.4.0"),sQuery(id+"F0.wireOp",EDGE,"E9.4.4.0"),sQuery(id+"F0.wireOp",EDGE,"E9.8.4.0"),sQuery(id+"F0.wireOp",EDGE,"E9.3.5.0"),sQuery(id+"F0.wireOp",EDGE,"E9.4.5.0"),sQuery(id+"F0.wireOp",EDGE,"E9.8.5.0"),sQuery(id+"F0.wireOp",EDGE,"E9.3.6.0"),sQuery(id+"F0.wireOp",EDGE,"E9.4.6.0"),sQuery(id+"F0.wireOp",EDGE,"E9.8.6.0"),sQuery(id+"F0.wireOp",EDGE,"E9.3.7.0"),sQuery(id+"F0.wireOp",EDGE,"E9.4.7.0"),sQuery(id+"F0.wireOp",EDGE,"E9.8.7.0"),sQuery(id+"F0.wireOp",EDGE,"E9.3.8.0"),sQuery(id+"F0.wireOp",EDGE,"E9.4.8.0"),sQuery(id+"F0.wireOp",EDGE,"E9.8.8.0"),sQuery(id+"F0.wireOp",EDGE,"E9.3.9.0"),sQuery(id+"F0.wireOp",EDGE,"E9.4.9.0"),sQuery(id+"F0.wireOp",EDGE,"E9.8.9.0"),sQuery(id+"F0.wireOp",EDGE,"E9.3.10.0"),sQuery(id+"F0.wireOp",EDGE,"E9.4.10.0"),sQuery(id+"F0.wireOp",EDGE,"E9.8.10.0"),sQuery(id+"F0.wireOp",EDGE,"E9.3.11.0"),sQuery(id+"F0.wireOp",EDGE,"E9.4.11.0"),sQuery(id+"F0.wireOp",EDGE,"E9.8.11.0"),sQuery(id+"F0.wireOp",EDGE,"E9.3.12.0"),sQuery(id+"F0.wireOp",EDGE,"E9.4.12.0"),sQuery(id+"F0.wireOp",EDGE,"E9.8.12.0"),sQuery(id+"F0.wireOp",EDGE,"E9.3.13.0"),sQuery(id+"F0.wireOp",EDGE,"E9.4.13.0"),sQuery(id+"F0.wireOp",EDGE,"E9.8.13.0"),sQuery(id+"F0.wireOp",EDGE,"E9.3.14.0"),sQuery(id+"F0.wireOp",EDGE,"E9.4.14.0"),sQuery(id+"F0.wireOp",EDGE,"E9.8.14.0"),sQuery(id+"F0.wireOp",EDGE,"E9.3.15.0"),sQuery(id+"F0.wireOp",EDGE,"E9.4.15.0"),sQuery(id+"F0.wireOp",EDGE,"E9.8.15.0"),sQuery(id+"F0.wireOp",EDGE,"E9.3.16.0"),sQuery(id+"F0.wireOp",EDGE,"E9.4.16.0"),sQuery(id+"F0.wireOp",EDGE,"E9.8.16.0"),sQuery(id+"F0.wireOp",EDGE,"E9.3.17.0"),sQuery(id+"F0.wireOp",EDGE,"E9.4.17.0"),sQuery(id+"F0.wireOp",EDGE,"E9.8.17.0"),sQuery(id+"F0.wireOp",EDGE,"E9.3.18.0"),sQuery(id+"F0.wireOp",EDGE,"E9.4.18.0"),sQuery(id+"F0.wireOp",EDGE,"E9.8.18.0"),sQuery(id+"F0.wireOp",EDGE,"E9.3.19.0"),sQuery(id+"F0.wireOp",EDGE,"E9.4.19.0"),sQuery(id+"F0.wireOp",EDGE,"E9.8.19.0"),sQuery(id+"F0.wireOp",EDGE,"E9.3.20.0"),sQuery(id+"F0.wireOp",EDGE,"E9.4.20.0"),sQuery(id+"F0.wireOp",EDGE,"E9.8.20.0"),sQuery(id+"F0.wireOp",EDGE,"E10"),sQuery(id+"F0.wireOp",EDGE,"E11.1.0"),sQuery(id+"F0.wireOp",EDGE,"E11.2.0"),sQuery(id+"F0.wireOp",EDGE,"E11.3.0"),sQuery(id+"F0.wireOp",EDGE,"E11.4.0"),sQuery(id+"F0.wireOp",EDGE,"E11.5.0"),sQuery(id+"F0.wireOp",EDGE,"E11.6.0"),sQuery(id+"F0.wireOp",EDGE,"E11.7.0"),sQuery(id+"F0.wireOp",EDGE,"E11.8.0"),sQuery(id+"F0.wireOp",EDGE,"E11.9.0"),sQuery(id+"F0.wireOp",EDGE,"E11.10.0"),sQuery(id+"F0.wireOp",EDGE,"E11.11.0"),sQuery(id+"F0.wireOp",EDGE,"E11.12.0"),sQuery(id+"F0.wireOp",EDGE,"E11.13.0"),sQuery(id+"F0.wireOp",EDGE,"E11.14.0"),sQuery(id+"F0.wireOp",EDGE,"E11.15.0"),sQuery(id+"F0.wireOp",EDGE,"E11.16.0"),sQuery(id+"F0.wireOp",EDGE,"E11.17.0"),sQuery(id+"F0.wireOp",EDGE,"E11.18.0"),sQuery(id+"F0.wireOp",EDGE,"E11.19.0"),sQuery(id+"F0.wireOp",EDGE,"E11.20.0")])]}),"instanceName":"1"}),"instanceName":"1"}),"instanceName":"1"});
            var Q1;
            Q1=makeQuery(id+"F19.opPattern","COPY",EDGE,{"derivedFrom":makeQuery(id+"F16.opPattern","COPY",EDGE,{"derivedFrom":makeQuery(id+"F13.opPattern","COPY",EDGE,{"derivedFrom":makeQuery(id+"F2.opExtrude","CAP_EDGE",EDGE,{"disambiguationData":[OSD([sQuery(id+"F0.wireOp",EDGE,"E1")])],"isStart":false}),"instanceName":"1"}),"instanceName":"1"}),"instanceName":"1"});
            transform(context, id + "F20", {"entities" : qUnion([Q0]), "transformType" : TransformType.ROTATION, "transformAxis" : qUnion([Q1]), "angle" : 4.3 * degree, "makeCopy" : false});
        }
        {
            var Q0;
            Q0=makeQuery(id+"F19.opPattern","COPY",BODY,{"derivedFrom":makeQuery(id+"F16.opPattern","COPY",BODY,{"derivedFrom":makeQuery(id+"F13.opPattern","COPY",BODY,{"derivedFrom":makeQuery(id+"F1.opExtrude","SWEPT_BODY",BODY,{"disambiguationData":[OSD([sQuery(id+"F0.wireOp",EDGE,"E0"),sQuery(id+"F0.wireOp",EDGE,"E1"),sQuery(id+"F0.wireOp",EDGE,"E3"),sQuery(id+"F0.wireOp",EDGE,"E5"),sQuery(id+"F0.wireOp",EDGE,"E7"),sQuery(id+"F0.wireOp",EDGE,"E8.1.3"),sQuery(id+"F0.wireOp",EDGE,"E8.1.4"),sQuery(id+"F0.wireOp",EDGE,"E8.1.5"),sQuery(id+"F0.wireOp",EDGE,"E8.2.3"),sQuery(id+"F0.wireOp",EDGE,"E8.2.4"),sQuery(id+"F0.wireOp",EDGE,"E8.2.5"),sQuery(id+"F0.wireOp",EDGE,"E9.11.3.0"),sQuery(id+"F0.wireOp",EDGE,"E9.15.3.0"),sQuery(id+"F0.wireOp",EDGE,"E9.19.3.0"),sQuery(id+"F0.wireOp",EDGE,"E9.11.4.0"),sQuery(id+"F0.wireOp",EDGE,"E9.15.4.0"),sQuery(id+"F0.wireOp",EDGE,"E9.19.4.0"),sQuery(id+"F0.wireOp",EDGE,"E9.11.5.0"),sQuery(id+"F0.wireOp",EDGE,"E9.15.5.0"),sQuery(id+"F0.wireOp",EDGE,"E9.19.5.0"),sQuery(id+"F0.wireOp",EDGE,"E9.11.6.0"),sQuery(id+"F0.wireOp",EDGE,"E9.15.6.0"),sQuery(id+"F0.wireOp",EDGE,"E9.19.6.0"),sQuery(id+"F0.wireOp",EDGE,"E9.11.7.0"),sQuery(id+"F0.wireOp",EDGE,"E9.15.7.0"),sQuery(id+"F0.wireOp",EDGE,"E9.19.7.0"),sQuery(id+"F0.wireOp",EDGE,"E9.11.8.0"),sQuery(id+"F0.wireOp",EDGE,"E9.15.8.0"),sQuery(id+"F0.wireOp",EDGE,"E9.19.8.0"),sQuery(id+"F0.wireOp",EDGE,"E9.11.9.0"),sQuery(id+"F0.wireOp",EDGE,"E9.15.9.0"),sQuery(id+"F0.wireOp",EDGE,"E9.19.9.0"),sQuery(id+"F0.wireOp",EDGE,"E9.11.10.0"),sQuery(id+"F0.wireOp",EDGE,"E9.15.10.0"),sQuery(id+"F0.wireOp",EDGE,"E9.19.10.0"),sQuery(id+"F0.wireOp",EDGE,"E9.11.11.0"),sQuery(id+"F0.wireOp",EDGE,"E9.15.11.0"),sQuery(id+"F0.wireOp",EDGE,"E9.19.11.0"),sQuery(id+"F0.wireOp",EDGE,"E9.11.12.0"),sQuery(id+"F0.wireOp",EDGE,"E9.15.12.0"),sQuery(id+"F0.wireOp",EDGE,"E9.19.12.0"),sQuery(id+"F0.wireOp",EDGE,"E9.11.13.0"),sQuery(id+"F0.wireOp",EDGE,"E9.15.13.0"),sQuery(id+"F0.wireOp",EDGE,"E9.19.13.0"),sQuery(id+"F0.wireOp",EDGE,"E9.11.14.0"),sQuery(id+"F0.wireOp",EDGE,"E9.15.14.0"),sQuery(id+"F0.wireOp",EDGE,"E9.19.14.0"),sQuery(id+"F0.wireOp",EDGE,"E9.11.15.0"),sQuery(id+"F0.wireOp",EDGE,"E9.15.15.0"),sQuery(id+"F0.wireOp",EDGE,"E9.19.15.0"),sQuery(id+"F0.wireOp",EDGE,"E9.11.16.0"),sQuery(id+"F0.wireOp",EDGE,"E9.15.16.0"),sQuery(id+"F0.wireOp",EDGE,"E9.19.16.0"),sQuery(id+"F0.wireOp",EDGE,"E9.11.17.0"),sQuery(id+"F0.wireOp",EDGE,"E9.15.17.0"),sQuery(id+"F0.wireOp",EDGE,"E9.19.17.0"),sQuery(id+"F0.wireOp",EDGE,"E9.11.18.0"),sQuery(id+"F0.wireOp",EDGE,"E9.15.18.0"),sQuery(id+"F0.wireOp",EDGE,"E9.19.18.0"),sQuery(id+"F0.wireOp",EDGE,"E9.11.19.0"),sQuery(id+"F0.wireOp",EDGE,"E9.15.19.0"),sQuery(id+"F0.wireOp",EDGE,"E9.19.19.0"),sQuery(id+"F0.wireOp",EDGE,"E9.11.20.0"),sQuery(id+"F0.wireOp",EDGE,"E9.15.20.0"),sQuery(id+"F0.wireOp",EDGE,"E9.19.20.0")])]}),"instanceName":"1"}),"instanceName":"1"}),"instanceName":"1"});
            var Q1;
            Q1=makeQuery(id+"F19.opPattern","COPY",EDGE,{"derivedFrom":makeQuery(id+"F16.opPattern","COPY",EDGE,{"derivedFrom":makeQuery(id+"F13.opPattern","COPY",EDGE,{"derivedFrom":makeQuery(id+"F1.opExtrude","CAP_EDGE",EDGE,{"disambiguationData":[OSD([sQuery(id+"F0.wireOp",EDGE,"E1")])],"isStart":false}),"instanceName":"1"}),"instanceName":"1"}),"instanceName":"1"});
            transform(context, id + "F21", {"entities" : qUnion([Q0]), "transformType" : TransformType.ROTATION, "transformAxis" : qUnion([Q1]), "angle" : 4.3 * degree, "oppositeDirection" : true, "makeCopy" : false});
        }
    });
